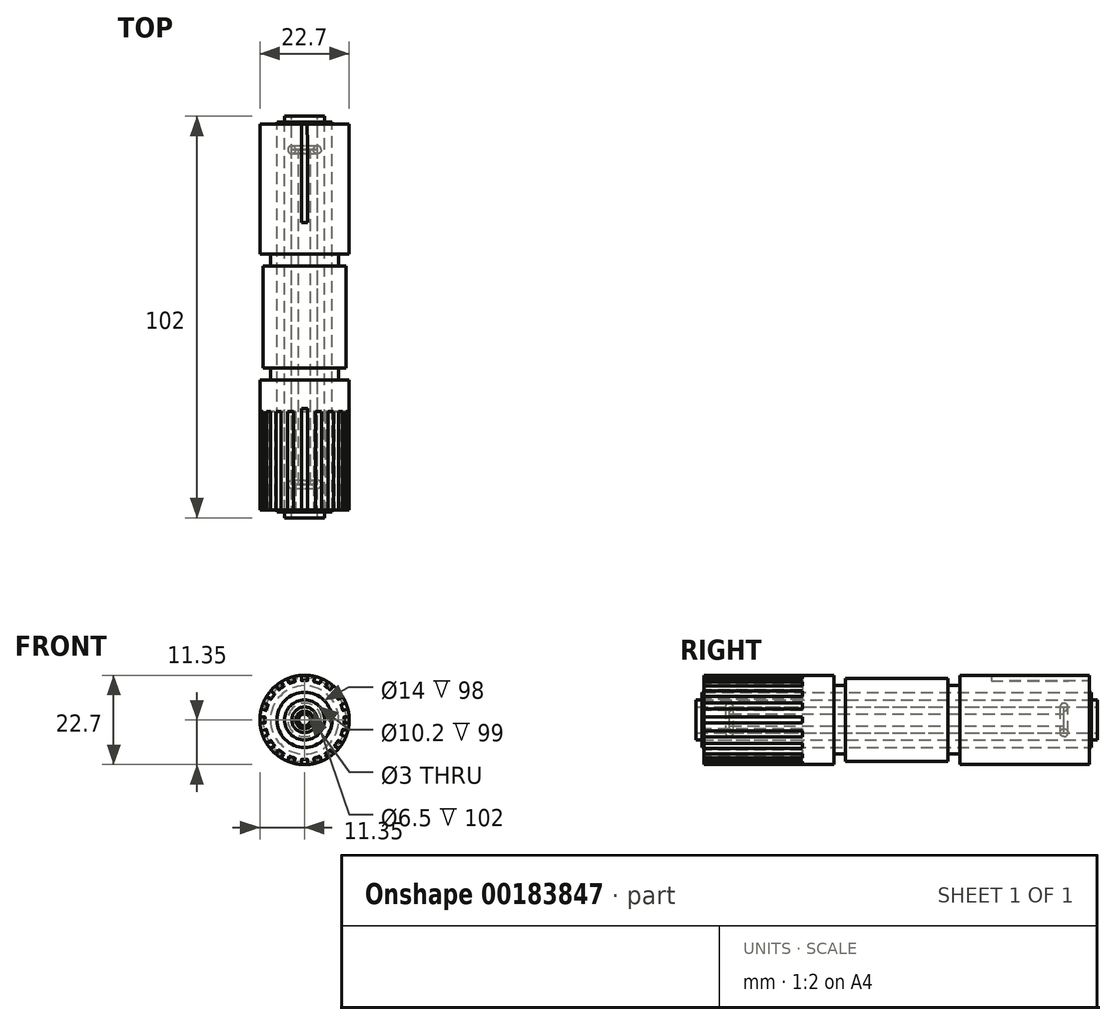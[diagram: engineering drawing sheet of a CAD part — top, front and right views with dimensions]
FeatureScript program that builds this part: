
annotation { "Feature Type Name" : "Feature", "Feature Type Description" : "" }
export const myFeature = defineFeature(function(context is Context, id is Id, definition is map)
    precondition{}
    {
        {
            var Q0;
            Q0=qCreatedBy(makeId("Front.planeOp"),FACE);
            var sketch = newSketch(context, id + "F0", { "sketchPlane" : qUnion([Q0])});
            skCircle(sketch, "E0", {"center": v(0, 0) * mm, "radius": 5.1 * mm});
            skCircle(sketch, "E1", {"center": v(0, 0) * mm, "radius": 7 * mm});
            skCircle(sketch, "E2", {"center": v(0, 0) * mm, "radius": 11.35 * mm});
            skCircle(sketch, "E3", {"center": v(0, 0) * mm, "radius": 8.7 * mm});
            skCircle(sketch, "E4", {"center": v(0, 0) * mm, "radius": 10.6 * mm});
            skCircle(sketch, "E5", {"center": v(0, 0) * mm, "radius": 10 * mm});
            skCircle(sketch, "E6", {"center": v(0, 0) * mm, "radius": 1.5 * mm});
            skCircle(sketch, "E7", {"center": v(0, 0) * mm, "radius": 3.25 * mm});
            skSolve(sketch);
        }
        {
            var Q0;
            Q0=makeQuery(id+"F0.imprint","IMPRINT",FACE,{"disambiguationData":[TD([[makeQuery(id+"F0.imprint","IMPRINT",EDGE,{"derivedFrom":sQuery(id+"F0.wireOp",EDGE,"E0")}),1.0]])]});
            extrude(context, id + "F1", {"entities" : qUnion([Q0]), "endBound" : BoundingType.SYMMETRIC, "depth" : 102 * mm});
        }
        {
            var Q0;
            Q0=makeQuery(id+"F0.imprint","IMPRINT",FACE,{"disambiguationData":[TD([[makeQuery(id+"F0.imprint","IMPRINT",EDGE,{"derivedFrom":sQuery(id+"F0.wireOp",EDGE,"E0")}),-1.0]])]});
            extrude(context, id + "F2", {"entities" : qUnion([Q0]), "endBound" : BoundingType.SYMMETRIC, "depth" : 99 * mm});
        }
        {
            var Q0;
            Q0=makeQuery(id+"F0.imprint","IMPRINT",FACE,{"disambiguationData":[TD([[makeQuery(id+"F0.imprint","IMPRINT",EDGE,{"derivedFrom":sQuery(id+"F0.wireOp",EDGE,"E6")}),-1.0]])]});
            extrude(context, id + "F3", {"entities" : qUnion([Q0]), "endBound" : BoundingType.SYMMETRIC, "depth" : 85 * mm});
        }
        {
            var Q0;
            Q0=makeQuery(id+"F0.imprint","IMPRINT",FACE,{"disambiguationData":[TD([[makeQuery(id+"F0.imprint","IMPRINT",EDGE,{"derivedFrom":sQuery(id+"F0.wireOp",EDGE,"E4")}),1.0]])]});
            var Q1;
            Q1=makeQuery(id+"F0.imprint","IMPRINT",FACE,{"disambiguationData":[TD([[makeQuery(id+"F0.imprint","IMPRINT",EDGE,{"derivedFrom":sQuery(id+"F0.wireOp",EDGE,"E3")}),-1.0]])]});
            var Q2;
            Q2=makeQuery(id+"F0.imprint","IMPRINT",FACE,{"disambiguationData":[TD([[makeQuery(id+"F0.imprint","IMPRINT",EDGE,{"derivedFrom":sQuery(id+"F0.wireOp",EDGE,"E1")}),-1.0]])]});
            var Q3;
            Q3=makeQuery(id+"F0.imprint","IMPRINT",FACE,{"disambiguationData":[TD([[makeQuery(id+"F0.imprint","IMPRINT",EDGE,{"derivedFrom":sQuery(id+"F0.wireOp",EDGE,"E2")}),1.0]])]});
            extrude(context, id + "F4", {"entities" : qUnion([Q0, Q1, Q2, Q3]), "endBound" : BoundingType.SYMMETRIC, "depth" : 98 * mm});
        }
        {
            var Q0;
            Q0=qCreatedBy(makeId("Front.planeOp"),FACE);
            var sketch = newSketch(context, id + "F5", { "sketchPlane" : qUnion([Q0])});
            skCircle(sketch, "E8.0", {"center": v(0, 0) * mm, "radius": 11.35 * mm});
            skCircle(sketch, "E9.0", {"center": v(0, 0) * mm, "radius": 8.7 * mm});
            skSolve(sketch);
        }
        {
            var Q0;
            Q0 = qSketchRegion(id + "F5", true);
            extrude(context, id + "F6", {"entities" : qUnion([Q0]), "operationType" : NewBodyOperationType.REMOVE, "endBound" : BoundingType.SYMMETRIC, "oppositeDirection" : true, "depth" : 32 * mm});
        }
        {
            var Q0;
            Q0=qCreatedBy(makeId("Front.planeOp"),FACE);
            var sketch = newSketch(context, id + "F7", { "sketchPlane" : qUnion([Q0])});
            skCircle(sketch, "E10.0", {"center": v(0, 0) * mm, "radius": 10.6 * mm});
            skCircle(sketch, "E11.0", {"center": v(0, 0) * mm, "radius": 8.7 * mm});
            skSolve(sketch);
        }
        {
            var Q0;
            Q0 = qSketchRegion(id + "F7", true);
            extrude(context, id + "F8", {"entities" : qUnion([Q0]), "operationType" : NewBodyOperationType.ADD, "endBound" : BoundingType.SYMMETRIC, "depth" : 26 * mm});
        }
        {
            var Q0;
            Q0=makeQuery(id+"F3.opExtrude","CAP_FACE",FACE,{"disambiguationData":[OSD([sQuery(id+"F0.wireOp",EDGE,"E6"),sQuery(id+"F0.wireOp",EDGE,"E7")])],"isStart":false});
            cPlane(context, id + "F9", {"entities" : qUnion([Q0]), "cplaneType" : CPlaneType.OFFSET, "offset" : 0 * mm, "width" : 150 * mm, "height" : 150 * mm});
        }
        {
            var Q0;
            Q0=qCreatedBy(id+"F9.planeOp",FACE);
            var sketch = newSketch(context, id + "F10", { "sketchPlane" : qUnion([Q0])});
            skCircle(sketch, "E12.0", {"center": v(0, 0) * mm, "radius": 3.25 * mm, "construction": true});
            skSolve(sketch);
        }
        {
            var Q0;
            Q0=qCreatedBy(makeId("Right.planeOp"),FACE);
            var sketch = newSketch(context, id + "F11", { "sketchPlane" : qUnion([Q0])});
            skLineSegment(sketch, "E13.0", {"start": v(-42.5, -3.25) * mm, "end": v(-42.5, 3.25) * mm, "construction": true});
            skCircle(sketch, "E14", {"center": v(-42.5, 3.25) * mm, "radius": 1 * mm});
            skSolve(sketch);
        }
        {
            var Q0;
            Q0 = qSketchRegion(id + "F11", true);
            var Q1;
            Q1=sQuery(id+"F11.wireOp",EDGE,"E14");
            var Q2;
            Q2=sQuery(id+"F10.wireOp",EDGE,"E12.0");
            revolve(context, id + "F12", {"entities" : qUnion([Q0]), "surfaceEntities" : qUnion([Q1]), "axis" : qUnion([Q2]), "revolveType" : RevolveType.FULL});
        }
        {
            var Q0;
            Q0=makeQuery(id+"F12.opRevolve","SWEPT_BODY",BODY,{"disambiguationData":[OSD([sQuery(id+"F11.wireOp",EDGE,"E14")])]});
            var Q1;
            Q1=qCreatedBy(makeId("Front.planeOp"),FACE);
            mirror(context, id + "F13", {"entities" : qUnion([Q0]), "mirrorPlane" : qUnion([Q1])});
        }
        {
            var Q0;
            Q0=makeQuery(id+"F4.opExtrude","CAP_FACE",FACE,{"disambiguationData":[OSD([sQuery(id+"F0.wireOp",EDGE,"E1"),sQuery(id+"F0.wireOp",EDGE,"E2")])],"isStart":false});
            cPlane(context, id + "F14", {"entities" : qUnion([Q0]), "cplaneType" : CPlaneType.OFFSET, "offset" : 0 * mm, "width" : 150 * mm, "height" : 150 * mm});
        }
        {
            var Q0;
            Q0=qCreatedBy(id+"F14.planeOp",FACE);
            var sketch = newSketch(context, id + "F15", { "sketchPlane" : qUnion([Q0])});
            skCircle(sketch, "E15.0", {"center": v(0, 0) * mm, "radius": 11.35 * mm, "construction": true});
            skCircle(sketch, "E16.0", {"center": v(0, 0) * mm, "radius": 10 * mm, "construction": true});
            skSolve(sketch);
        }
        {
            var Q0;
            Q0=qCreatedBy(makeId("Right.planeOp"),FACE);
            var sketch = newSketch(context, id + "F16", { "sketchPlane" : qUnion([Q0])});
            skLineSegment(sketch, "E17", {"start": v(-49, 10) * mm, "end": v(-49, 11.35) * mm});
            skPoint(sketch, "E18.0.start.orphan", {"position": v(-49, -10) * mm});
            skLineSegment(sketch, "E19", {"start": v(-49, 10.67) * mm, "end": v(-13.63, 12.53) * mm});
            skSolve(sketch);
        }
        {
            var Q0;
            Q0=qCreatedBy(id+"F14.planeOp",FACE);
            var sketch = newSketch(context, id + "F17", { "sketchPlane" : qUnion([Q0])});
            skLineSegment(sketch, "E20.0", {"start": v(0, 10) * mm, "end": v(0, 11.35) * mm, "construction": true});
            skPoint(sketch, "E21.middle", {"position": v(0, 10.68) * mm});
            skLineSegment(sketch, "E22.left", {"start": v(0.8, 11.32) * mm, "end": v(0.8, 10.08) * mm});
            skLineSegment(sketch, "E22.right", {"start": v(-0.8, 11.32) * mm, "end": v(-0.8, 10.08) * mm});
            skArc(sketch, "E23.0", {"start": v(0.7, 9.98) * mm, "mid": v(0, 10) * mm, "end": v(-0.7, 9.98) * mm});
            skPoint(sketch, "E24.orphan", {"position": v(-0.8, 9.9) * mm});
            skPoint(sketch, "E25.orphan", {"position": v(0.8, 9.9) * mm});
            skArc(sketch, "E26.0", {"start": v(0.8, 11.32) * mm, "mid": v(0, 11.35) * mm, "end": v(-0.8, 11.32) * mm});
            skPoint(sketch, "E27.orphan", {"position": v(-0.8, 11.44) * mm});
            skPoint(sketch, "E28.orphan", {"position": v(0.8, 11.44) * mm});
            skPoint(sketch, "E29.visualSharp", {"position": v(0.8, 9.97) * mm});
            skArc(sketch, "E29.filletArc", {"start": v(0.7, 9.98) * mm, "mid": v(0.77, 10) * mm, "end": v(0.8, 10.08) * mm});
            skPoint(sketch, "E30.visualSharp", {"position": v(-0.8, 9.97) * mm});
            skArc(sketch, "E30.filletArc", {"start": v(-0.8, 10.08) * mm, "mid": v(-0.77, 10) * mm, "end": v(-0.7, 9.98) * mm});
            skLineSegment(sketch, "E31.1.0", {"start": v(-4.26, 10.52) * mm, "end": v(-3.87, 9.34) * mm});
            skArc(sketch, "E31.1.1", {"start": v(-2.74, 11.01) * mm, "mid": v(-3.5, 10.8) * mm, "end": v(-4.26, 10.52) * mm});
            skLineSegment(sketch, "E31.1.2", {"start": v(-2.74, 11.01) * mm, "end": v(-2.35, 9.83) * mm});
            skArc(sketch, "E31.1.3", {"start": v(-2.42, 9.7) * mm, "mid": v(-3.1, 9.51) * mm, "end": v(-3.74, 9.27) * mm});
            skLineSegment(sketch, "E31.2.0", {"start": v(-7.3, 8.69) * mm, "end": v(-6.57, 7.68) * mm});
            skArc(sketch, "E31.2.1", {"start": v(-6, 9.63) * mm, "mid": v(-6.67, 9.18) * mm, "end": v(-7.3, 8.69) * mm});
            skLineSegment(sketch, "E31.2.2", {"start": v(-6, 9.63) * mm, "end": v(-5.28, 8.62) * mm});
            skArc(sketch, "E31.2.3", {"start": v(-5.3, 8.48) * mm, "mid": v(-5.88, 8.1) * mm, "end": v(-6.42, 7.66) * mm});
            skLineSegment(sketch, "E31.3.0", {"start": v(-9.63, 6) * mm, "end": v(-8.62, 5.28) * mm});
            skArc(sketch, "E31.3.1", {"start": v(-8.69, 7.3) * mm, "mid": v(-9.18, 6.67) * mm, "end": v(-9.63, 6) * mm});
            skLineSegment(sketch, "E31.3.2", {"start": v(-8.69, 7.3) * mm, "end": v(-7.68, 6.57) * mm});
            skArc(sketch, "E31.3.3", {"start": v(-7.66, 6.42) * mm, "mid": v(-8.1, 5.88) * mm, "end": v(-8.48, 5.3) * mm});
            skLineSegment(sketch, "E31.4.0", {"start": v(-11.01, 2.74) * mm, "end": v(-9.83, 2.35) * mm});
            skArc(sketch, "E31.4.1", {"start": v(-10.52, 4.26) * mm, "mid": v(-10.8, 3.5) * mm, "end": v(-11.01, 2.74) * mm});
            skLineSegment(sketch, "E31.4.2", {"start": v(-10.52, 4.26) * mm, "end": v(-9.34, 3.87) * mm});
            skArc(sketch, "E31.4.3", {"start": v(-9.27, 3.74) * mm, "mid": v(-9.51, 3.1) * mm, "end": v(-9.7, 2.42) * mm});
            skLineSegment(sketch, "E31.5.0", {"start": v(-11.32, -0.8) * mm, "end": v(-10.08, -0.8) * mm});
            skArc(sketch, "E31.5.1", {"start": v(-11.32, 0.8) * mm, "mid": v(-11.35, 0) * mm, "end": v(-11.32, -0.8) * mm});
            skLineSegment(sketch, "E31.5.2", {"start": v(-11.32, 0.8) * mm, "end": v(-10.08, 0.8) * mm});
            skArc(sketch, "E31.5.3", {"start": v(-9.98, 0.7) * mm, "mid": v(-10, 0) * mm, "end": v(-9.98, -0.7) * mm});
            skLineSegment(sketch, "E31.6.0", {"start": v(-10.52, -4.26) * mm, "end": v(-9.34, -3.87) * mm});
            skArc(sketch, "E31.6.1", {"start": v(-11.01, -2.74) * mm, "mid": v(-10.8, -3.5) * mm, "end": v(-10.52, -4.26) * mm});
            skLineSegment(sketch, "E31.6.2", {"start": v(-11.01, -2.74) * mm, "end": v(-9.83, -2.35) * mm});
            skArc(sketch, "E31.6.3", {"start": v(-9.7, -2.42) * mm, "mid": v(-9.51, -3.1) * mm, "end": v(-9.27, -3.74) * mm});
            skLineSegment(sketch, "E31.7.0", {"start": v(-8.69, -7.3) * mm, "end": v(-7.68, -6.57) * mm});
            skArc(sketch, "E31.7.1", {"start": v(-9.63, -6) * mm, "mid": v(-9.18, -6.67) * mm, "end": v(-8.69, -7.3) * mm});
            skLineSegment(sketch, "E31.7.2", {"start": v(-9.63, -6) * mm, "end": v(-8.62, -5.28) * mm});
            skArc(sketch, "E31.7.3", {"start": v(-8.48, -5.3) * mm, "mid": v(-8.1, -5.88) * mm, "end": v(-7.66, -6.42) * mm});
            skLineSegment(sketch, "E31.8.0", {"start": v(-6, -9.63) * mm, "end": v(-5.28, -8.62) * mm});
            skArc(sketch, "E31.8.1", {"start": v(-7.3, -8.69) * mm, "mid": v(-6.67, -9.18) * mm, "end": v(-6, -9.63) * mm});
            skLineSegment(sketch, "E31.8.2", {"start": v(-7.3, -8.69) * mm, "end": v(-6.57, -7.68) * mm});
            skArc(sketch, "E31.8.3", {"start": v(-6.42, -7.66) * mm, "mid": v(-5.88, -8.1) * mm, "end": v(-5.3, -8.48) * mm});
            skLineSegment(sketch, "E31.9.0", {"start": v(-2.74, -11.01) * mm, "end": v(-2.35, -9.83) * mm});
            skArc(sketch, "E31.9.1", {"start": v(-4.26, -10.52) * mm, "mid": v(-3.5, -10.8) * mm, "end": v(-2.74, -11.01) * mm});
            skLineSegment(sketch, "E31.9.2", {"start": v(-4.26, -10.52) * mm, "end": v(-3.87, -9.34) * mm});
            skArc(sketch, "E31.9.3", {"start": v(-3.74, -9.27) * mm, "mid": v(-3.1, -9.51) * mm, "end": v(-2.42, -9.7) * mm});
            skLineSegment(sketch, "E31.10.0", {"start": v(0.8, -11.32) * mm, "end": v(0.8, -10.08) * mm});
            skArc(sketch, "E31.10.1", {"start": v(-0.8, -11.32) * mm, "mid": v(0, -11.35) * mm, "end": v(0.8, -11.32) * mm});
            skLineSegment(sketch, "E31.10.2", {"start": v(-0.8, -11.32) * mm, "end": v(-0.8, -10.08) * mm});
            skArc(sketch, "E31.10.3", {"start": v(-0.7, -9.98) * mm, "mid": v(0, -10) * mm, "end": v(0.7, -9.98) * mm});
            skLineSegment(sketch, "E31.11.0", {"start": v(4.26, -10.52) * mm, "end": v(3.87, -9.34) * mm});
            skArc(sketch, "E31.11.1", {"start": v(2.74, -11.01) * mm, "mid": v(3.5, -10.8) * mm, "end": v(4.26, -10.52) * mm});
            skLineSegment(sketch, "E31.11.2", {"start": v(2.74, -11.01) * mm, "end": v(2.35, -9.83) * mm});
            skArc(sketch, "E31.11.3", {"start": v(2.42, -9.7) * mm, "mid": v(3.1, -9.51) * mm, "end": v(3.74, -9.27) * mm});
            skLineSegment(sketch, "E31.12.0", {"start": v(7.3, -8.69) * mm, "end": v(6.57, -7.68) * mm});
            skArc(sketch, "E31.12.1", {"start": v(6, -9.63) * mm, "mid": v(6.67, -9.18) * mm, "end": v(7.3, -8.69) * mm});
            skLineSegment(sketch, "E31.12.2", {"start": v(6, -9.63) * mm, "end": v(5.28, -8.62) * mm});
            skArc(sketch, "E31.12.3", {"start": v(5.3, -8.48) * mm, "mid": v(5.88, -8.1) * mm, "end": v(6.42, -7.66) * mm});
            skLineSegment(sketch, "E31.13.0", {"start": v(9.63, -6) * mm, "end": v(8.62, -5.28) * mm});
            skArc(sketch, "E31.13.1", {"start": v(8.69, -7.3) * mm, "mid": v(9.18, -6.67) * mm, "end": v(9.63, -6) * mm});
            skLineSegment(sketch, "E31.13.2", {"start": v(8.69, -7.3) * mm, "end": v(7.68, -6.57) * mm});
            skArc(sketch, "E31.13.3", {"start": v(7.66, -6.42) * mm, "mid": v(8.1, -5.88) * mm, "end": v(8.48, -5.3) * mm});
            skLineSegment(sketch, "E31.14.0", {"start": v(11.01, -2.74) * mm, "end": v(9.83, -2.35) * mm});
            skArc(sketch, "E31.14.1", {"start": v(10.52, -4.26) * mm, "mid": v(10.8, -3.5) * mm, "end": v(11.01, -2.74) * mm});
            skLineSegment(sketch, "E31.14.2", {"start": v(10.52, -4.26) * mm, "end": v(9.34, -3.87) * mm});
            skArc(sketch, "E31.14.3", {"start": v(9.27, -3.74) * mm, "mid": v(9.51, -3.1) * mm, "end": v(9.7, -2.42) * mm});
            skLineSegment(sketch, "E31.15.0", {"start": v(11.32, 0.8) * mm, "end": v(10.08, 0.8) * mm});
            skArc(sketch, "E31.15.1", {"start": v(11.32, -0.8) * mm, "mid": v(11.35, 0) * mm, "end": v(11.32, 0.8) * mm});
            skLineSegment(sketch, "E31.15.2", {"start": v(11.32, -0.8) * mm, "end": v(10.08, -0.8) * mm});
            skArc(sketch, "E31.15.3", {"start": v(9.98, -0.7) * mm, "mid": v(10, 0) * mm, "end": v(9.98, 0.7) * mm});
            skLineSegment(sketch, "E31.16.0", {"start": v(10.52, 4.26) * mm, "end": v(9.34, 3.87) * mm});
            skArc(sketch, "E31.16.1", {"start": v(11.01, 2.74) * mm, "mid": v(10.8, 3.5) * mm, "end": v(10.52, 4.26) * mm});
            skLineSegment(sketch, "E31.16.2", {"start": v(11.01, 2.74) * mm, "end": v(9.83, 2.35) * mm});
            skArc(sketch, "E31.16.3", {"start": v(9.7, 2.42) * mm, "mid": v(9.51, 3.1) * mm, "end": v(9.27, 3.74) * mm});
            skLineSegment(sketch, "E31.17.0", {"start": v(8.69, 7.3) * mm, "end": v(7.68, 6.57) * mm});
            skArc(sketch, "E31.17.1", {"start": v(9.63, 6) * mm, "mid": v(9.18, 6.67) * mm, "end": v(8.69, 7.3) * mm});
            skLineSegment(sketch, "E31.17.2", {"start": v(9.63, 6) * mm, "end": v(8.62, 5.28) * mm});
            skArc(sketch, "E31.17.3", {"start": v(8.48, 5.3) * mm, "mid": v(8.1, 5.88) * mm, "end": v(7.66, 6.42) * mm});
            skLineSegment(sketch, "E31.18.0", {"start": v(6, 9.63) * mm, "end": v(5.28, 8.62) * mm});
            skArc(sketch, "E31.18.1", {"start": v(7.3, 8.69) * mm, "mid": v(6.67, 9.18) * mm, "end": v(6, 9.63) * mm});
            skLineSegment(sketch, "E31.18.2", {"start": v(7.3, 8.69) * mm, "end": v(6.57, 7.68) * mm});
            skArc(sketch, "E31.18.3", {"start": v(6.42, 7.66) * mm, "mid": v(5.88, 8.1) * mm, "end": v(5.3, 8.48) * mm});
            skLineSegment(sketch, "E31.19.0", {"start": v(2.74, 11.01) * mm, "end": v(2.35, 9.83) * mm});
            skArc(sketch, "E31.19.1", {"start": v(4.26, 10.52) * mm, "mid": v(3.5, 10.8) * mm, "end": v(2.74, 11.01) * mm});
            skLineSegment(sketch, "E31.19.2", {"start": v(4.26, 10.52) * mm, "end": v(3.87, 9.34) * mm});
            skArc(sketch, "E31.19.3", {"start": v(3.74, 9.27) * mm, "mid": v(3.1, 9.51) * mm, "end": v(2.42, 9.7) * mm});
            skArc(sketch, "E32.1.0", {"start": v(-3.87, 9.34) * mm, "mid": v(-3.82, 9.28) * mm, "end": v(-3.74, 9.27) * mm});
            skArc(sketch, "E32.1.1", {"start": v(-2.42, 9.7) * mm, "mid": v(-2.36, 9.75) * mm, "end": v(-2.35, 9.83) * mm});
            skArc(sketch, "E32.2.0", {"start": v(-6.57, 7.68) * mm, "mid": v(-6.5, 7.64) * mm, "end": v(-6.42, 7.66) * mm});
            skArc(sketch, "E32.2.1", {"start": v(-5.3, 8.48) * mm, "mid": v(-5.26, 8.54) * mm, "end": v(-5.28, 8.62) * mm});
            skArc(sketch, "E32.3.0", {"start": v(-8.62, 5.28) * mm, "mid": v(-8.54, 5.26) * mm, "end": v(-8.48, 5.3) * mm});
            skArc(sketch, "E32.3.1", {"start": v(-7.66, 6.42) * mm, "mid": v(-7.64, 6.5) * mm, "end": v(-7.68, 6.57) * mm});
            skArc(sketch, "E32.4.0", {"start": v(-9.83, 2.35) * mm, "mid": v(-9.75, 2.36) * mm, "end": v(-9.7, 2.42) * mm});
            skArc(sketch, "E32.4.1", {"start": v(-9.27, 3.74) * mm, "mid": v(-9.28, 3.82) * mm, "end": v(-9.34, 3.87) * mm});
            skArc(sketch, "E32.5.0", {"start": v(-10.08, -0.8) * mm, "mid": v(-10, -0.77) * mm, "end": v(-9.98, -0.7) * mm});
            skArc(sketch, "E32.5.1", {"start": v(-9.98, 0.7) * mm, "mid": v(-10, 0.77) * mm, "end": v(-10.08, 0.8) * mm});
            skArc(sketch, "E32.6.0", {"start": v(-9.34, -3.87) * mm, "mid": v(-9.28, -3.82) * mm, "end": v(-9.27, -3.74) * mm});
            skArc(sketch, "E32.6.1", {"start": v(-9.7, -2.42) * mm, "mid": v(-9.75, -2.36) * mm, "end": v(-9.83, -2.35) * mm});
            skArc(sketch, "E32.7.0", {"start": v(-7.68, -6.57) * mm, "mid": v(-7.64, -6.5) * mm, "end": v(-7.66, -6.42) * mm});
            skArc(sketch, "E32.7.1", {"start": v(-8.48, -5.3) * mm, "mid": v(-8.54, -5.26) * mm, "end": v(-8.62, -5.28) * mm});
            skArc(sketch, "E32.8.0", {"start": v(-5.28, -8.62) * mm, "mid": v(-5.26, -8.54) * mm, "end": v(-5.3, -8.48) * mm});
            skArc(sketch, "E32.8.1", {"start": v(-6.42, -7.66) * mm, "mid": v(-6.5, -7.64) * mm, "end": v(-6.57, -7.68) * mm});
            skArc(sketch, "E32.9.0", {"start": v(-2.35, -9.83) * mm, "mid": v(-2.36, -9.75) * mm, "end": v(-2.42, -9.7) * mm});
            skArc(sketch, "E32.9.1", {"start": v(-3.74, -9.27) * mm, "mid": v(-3.82, -9.28) * mm, "end": v(-3.87, -9.34) * mm});
            skArc(sketch, "E32.10.0", {"start": v(0.8, -10.08) * mm, "mid": v(0.77, -10) * mm, "end": v(0.7, -9.98) * mm});
            skArc(sketch, "E32.10.1", {"start": v(-0.7, -9.98) * mm, "mid": v(-0.77, -10) * mm, "end": v(-0.8, -10.08) * mm});
            skArc(sketch, "E32.11.0", {"start": v(3.87, -9.34) * mm, "mid": v(3.82, -9.28) * mm, "end": v(3.74, -9.27) * mm});
            skArc(sketch, "E32.11.1", {"start": v(2.42, -9.7) * mm, "mid": v(2.36, -9.75) * mm, "end": v(2.35, -9.83) * mm});
            skArc(sketch, "E32.12.0", {"start": v(6.57, -7.68) * mm, "mid": v(6.5, -7.64) * mm, "end": v(6.42, -7.66) * mm});
            skArc(sketch, "E32.12.1", {"start": v(5.3, -8.48) * mm, "mid": v(5.26, -8.54) * mm, "end": v(5.28, -8.62) * mm});
            skArc(sketch, "E32.13.0", {"start": v(8.62, -5.28) * mm, "mid": v(8.54, -5.26) * mm, "end": v(8.48, -5.3) * mm});
            skArc(sketch, "E32.13.1", {"start": v(7.66, -6.42) * mm, "mid": v(7.64, -6.5) * mm, "end": v(7.68, -6.57) * mm});
            skArc(sketch, "E32.14.0", {"start": v(9.83, -2.35) * mm, "mid": v(9.75, -2.36) * mm, "end": v(9.7, -2.42) * mm});
            skArc(sketch, "E32.14.1", {"start": v(9.27, -3.74) * mm, "mid": v(9.28, -3.82) * mm, "end": v(9.34, -3.87) * mm});
            skArc(sketch, "E32.15.0", {"start": v(10.08, 0.8) * mm, "mid": v(10, 0.77) * mm, "end": v(9.98, 0.7) * mm});
            skArc(sketch, "E32.15.1", {"start": v(9.98, -0.7) * mm, "mid": v(10, -0.77) * mm, "end": v(10.08, -0.8) * mm});
            skArc(sketch, "E32.16.0", {"start": v(9.34, 3.87) * mm, "mid": v(9.28, 3.82) * mm, "end": v(9.27, 3.74) * mm});
            skArc(sketch, "E32.16.1", {"start": v(9.7, 2.42) * mm, "mid": v(9.75, 2.36) * mm, "end": v(9.83, 2.35) * mm});
            skArc(sketch, "E32.17.0", {"start": v(7.68, 6.57) * mm, "mid": v(7.64, 6.5) * mm, "end": v(7.66, 6.42) * mm});
            skArc(sketch, "E32.17.1", {"start": v(8.48, 5.3) * mm, "mid": v(8.54, 5.26) * mm, "end": v(8.62, 5.28) * mm});
            skArc(sketch, "E32.18.0", {"start": v(5.28, 8.62) * mm, "mid": v(5.26, 8.54) * mm, "end": v(5.3, 8.48) * mm});
            skArc(sketch, "E32.18.1", {"start": v(6.42, 7.66) * mm, "mid": v(6.5, 7.64) * mm, "end": v(6.57, 7.68) * mm});
            skArc(sketch, "E32.19.0", {"start": v(2.35, 9.83) * mm, "mid": v(2.36, 9.75) * mm, "end": v(2.42, 9.7) * mm});
            skArc(sketch, "E32.19.1", {"start": v(3.74, 9.27) * mm, "mid": v(3.82, 9.28) * mm, "end": v(3.87, 9.34) * mm});
            skSolve(sketch);
        }
        {
            var Q0;
            Q0=makeQuery(id+"F17.imprint","IMPRINT",FACE,{"disambiguationData":[TD([[makeQuery(id+"F17.imprint","IMPRINT",EDGE,{"derivedFrom":sQuery(id+"F17.wireOp",EDGE,"E22.left")}),-1.0]])]});
            var Q1;
            Q1=sQuery(id+"F16.wireOp",EDGE,"E19");
            sweep(context, id + "F18", {"operationType" : NewBodyOperationType.REMOVE, "profiles" : qUnion([Q0]), "path" : qUnion([Q1]), "keepProfileOrientation" : true});
        }
        {
            var Q0;
            {var subQ0=sQuery(id+"F5.wireOp",EDGE,"E9.0");Q0=makeQuery(id+"F8.boolean.opBoolean","SPLIT",FACE,{"disambiguationData":[TD([makeQuery(id+"F6.boolean.opBoolean","COPY",FACE,{"derivedFrom":makeQuery(id+"F6.opExtrude","CAP_FACE",FACE,{"disambiguationData":[OSD([sQuery(id+"F5.wireOp",EDGE,"E8.0"),subQ0])],"isStart":true})})])],"derivedFrom":makeQuery(id+"F6.boolean.opBoolean","COPY",FACE,{"derivedFrom":makeQuery(id+"F6.opExtrude","SWEPT_FACE",FACE,{"disambiguationData":[OSD([subQ0])]})})});}
            var Q1;
            {var subQ0=sQuery(id+"F5.wireOp",EDGE,"E9.0");Q1=makeQuery(id+"F8.boolean.opBoolean","SPLIT",FACE,{"disambiguationData":[TD([makeQuery(id+"F6.boolean.opBoolean","COPY",FACE,{"derivedFrom":makeQuery(id+"F6.opExtrude","CAP_FACE",FACE,{"disambiguationData":[OSD([sQuery(id+"F5.wireOp",EDGE,"E8.0"),subQ0])],"isStart":false})})])],"derivedFrom":makeQuery(id+"F6.boolean.opBoolean","COPY",FACE,{"derivedFrom":makeQuery(id+"F6.opExtrude","SWEPT_FACE",FACE,{"disambiguationData":[OSD([subQ0])]})})});}
            fillet(context, id + "F19", {"entities" : qUnion([Q0, Q1]), "radius" : 0.2 * mm, "tangentPropagation" : true, "allowEdgeOverflow" : false});
        }
        {
            var Q0;
            Q0=makeQuery(id+"F17.imprint","IMPRINT",FACE,{"disambiguationData":[TD([[makeQuery(id+"F17.imprint","IMPRINT",EDGE,{"derivedFrom":sQuery(id+"F17.wireOp",EDGE,"E31.3.0")}),1.0]])]});
            var Q1;
            Q1=makeQuery(id+"F17.imprint","IMPRINT",FACE,{"disambiguationData":[TD([[makeQuery(id+"F17.imprint","IMPRINT",EDGE,{"derivedFrom":sQuery(id+"F17.wireOp",EDGE,"E31.4.0")}),1.0]])]});
            var Q2;
            Q2=makeQuery(id+"F17.imprint","IMPRINT",FACE,{"disambiguationData":[TD([[makeQuery(id+"F17.imprint","IMPRINT",EDGE,{"derivedFrom":sQuery(id+"F17.wireOp",EDGE,"E31.5.0")}),1.0]])]});
            var Q3;
            Q3=makeQuery(id+"F17.imprint","IMPRINT",FACE,{"disambiguationData":[TD([[makeQuery(id+"F17.imprint","IMPRINT",EDGE,{"derivedFrom":sQuery(id+"F17.wireOp",EDGE,"E31.6.0")}),1.0]])]});
            var Q4;
            Q4=makeQuery(id+"F17.imprint","IMPRINT",FACE,{"disambiguationData":[TD([[makeQuery(id+"F17.imprint","IMPRINT",EDGE,{"derivedFrom":sQuery(id+"F17.wireOp",EDGE,"E31.7.0")}),1.0]])]});
            var Q5;
            Q5=makeQuery(id+"F17.imprint","IMPRINT",FACE,{"disambiguationData":[TD([[makeQuery(id+"F17.imprint","IMPRINT",EDGE,{"derivedFrom":sQuery(id+"F17.wireOp",EDGE,"E31.8.0")}),1.0]])]});
            var Q6;
            Q6=makeQuery(id+"F17.imprint","IMPRINT",FACE,{"disambiguationData":[TD([[makeQuery(id+"F17.imprint","IMPRINT",EDGE,{"derivedFrom":sQuery(id+"F17.wireOp",EDGE,"E31.9.0")}),1.0]])]});
            var Q7;
            Q7=makeQuery(id+"F17.imprint","IMPRINT",FACE,{"disambiguationData":[TD([[makeQuery(id+"F17.imprint","IMPRINT",EDGE,{"derivedFrom":sQuery(id+"F17.wireOp",EDGE,"E31.10.0")}),1.0]])]});
            var Q8;
            Q8=makeQuery(id+"F17.imprint","IMPRINT",FACE,{"disambiguationData":[TD([[makeQuery(id+"F17.imprint","IMPRINT",EDGE,{"derivedFrom":sQuery(id+"F17.wireOp",EDGE,"E31.11.0")}),1.0]])]});
            var Q9;
            Q9=makeQuery(id+"F17.imprint","IMPRINT",FACE,{"disambiguationData":[TD([[makeQuery(id+"F17.imprint","IMPRINT",EDGE,{"derivedFrom":sQuery(id+"F17.wireOp",EDGE,"E31.12.0")}),1.0]])]});
            var Q10;
            Q10=makeQuery(id+"F17.imprint","IMPRINT",FACE,{"disambiguationData":[TD([[makeQuery(id+"F17.imprint","IMPRINT",EDGE,{"derivedFrom":sQuery(id+"F17.wireOp",EDGE,"E31.13.0")}),1.0]])]});
            var Q11;
            Q11=makeQuery(id+"F17.imprint","IMPRINT",FACE,{"disambiguationData":[TD([[makeQuery(id+"F17.imprint","IMPRINT",EDGE,{"derivedFrom":sQuery(id+"F17.wireOp",EDGE,"E31.14.0")}),1.0]])]});
            var Q12;
            Q12=makeQuery(id+"F17.imprint","IMPRINT",FACE,{"disambiguationData":[TD([[makeQuery(id+"F17.imprint","IMPRINT",EDGE,{"derivedFrom":sQuery(id+"F17.wireOp",EDGE,"E31.15.0")}),1.0]])]});
            var Q13;
            Q13=makeQuery(id+"F17.imprint","IMPRINT",FACE,{"disambiguationData":[TD([[makeQuery(id+"F17.imprint","IMPRINT",EDGE,{"derivedFrom":sQuery(id+"F17.wireOp",EDGE,"E31.16.0")}),1.0]])]});
            var Q14;
            Q14=makeQuery(id+"F17.imprint","IMPRINT",FACE,{"disambiguationData":[TD([[makeQuery(id+"F17.imprint","IMPRINT",EDGE,{"derivedFrom":sQuery(id+"F17.wireOp",EDGE,"E31.17.0")}),1.0]])]});
            var Q15;
            Q15=makeQuery(id+"F17.imprint","IMPRINT",FACE,{"disambiguationData":[TD([[makeQuery(id+"F17.imprint","IMPRINT",EDGE,{"derivedFrom":sQuery(id+"F17.wireOp",EDGE,"E31.18.0")}),1.0]])]});
            var Q16;
            Q16=makeQuery(id+"F17.imprint","IMPRINT",FACE,{"disambiguationData":[TD([[makeQuery(id+"F17.imprint","IMPRINT",EDGE,{"derivedFrom":sQuery(id+"F17.wireOp",EDGE,"E31.19.0")}),1.0]])]});
            var Q17;
            Q17=makeQuery(id+"F17.imprint","IMPRINT",FACE,{"disambiguationData":[TD([[makeQuery(id+"F17.imprint","IMPRINT",EDGE,{"derivedFrom":sQuery(id+"F17.wireOp",EDGE,"E31.1.0")}),1.0]])]});
            var Q18;
            Q18=makeQuery(id+"F17.imprint","IMPRINT",FACE,{"disambiguationData":[TD([[makeQuery(id+"F17.imprint","IMPRINT",EDGE,{"derivedFrom":sQuery(id+"F17.wireOp",EDGE,"E31.2.0")}),1.0]])]});
            extrude(context, id + "F20", {"entities" : qUnion([Q0, Q1, Q2, Q3, Q4, Q5, Q6, Q7, Q8, Q9, Q10, Q11, Q12, Q13, Q14, Q15, Q16, Q17, Q18]), "operationType" : NewBodyOperationType.REMOVE, "oppositeDirection" : true, "depth" : 25 * mm});
        }
        {
            var Q0;
            Q0=makeQuery(id+"F4.opExtrude","CAP_FACE",FACE,{"disambiguationData":[OSD([sQuery(id+"F0.wireOp",EDGE,"E1"),sQuery(id+"F0.wireOp",EDGE,"E2")])],"isStart":true});
            var sketch = newSketch(context, id + "F21", { "sketchPlane" : qUnion([Q0])});
            skLineSegment(sketch, "E33.0", {"start": v(0.8, 11.32) * mm, "end": v(0.8, 10.08) * mm});
            skArc(sketch, "E33.1", {"start": v(2.74, 11.01) * mm, "mid": v(3.5, 10.8) * mm, "end": v(4.26, 10.52) * mm});
            skArc(sketch, "E33.2", {"start": v(-6.42, 7.66) * mm, "mid": v(-5.88, 8.1) * mm, "end": v(-5.3, 8.48) * mm});
            skLineSegment(sketch, "E33.3", {"start": v(8.69, 7.3) * mm, "end": v(7.68, 6.57) * mm});
            skArc(sketch, "E33.4", {"start": v(6, 9.63) * mm, "mid": v(6.67, 9.18) * mm, "end": v(7.3, 8.69) * mm});
            skLineSegment(sketch, "E33.5", {"start": v(0.8, -11.32) * mm, "end": v(0.8, -10.08) * mm});
            skLineSegment(sketch, "E33.6", {"start": v(-2.74, 11.01) * mm, "end": v(-2.35, 9.83) * mm});
            skLineSegment(sketch, "E33.7", {"start": v(-10.52, -4.26) * mm, "end": v(-9.34, -3.87) * mm});
            skLineSegment(sketch, "E33.8", {"start": v(11.01, -2.74) * mm, "end": v(9.83, -2.35) * mm});
            skArc(sketch, "E33.9", {"start": v(5.3, 8.48) * mm, "mid": v(5.88, 8.1) * mm, "end": v(6.42, 7.66) * mm});
            skLineSegment(sketch, "E33.10", {"start": v(2.74, 11.01) * mm, "end": v(2.35, 9.83) * mm});
            skLineSegment(sketch, "E33.11", {"start": v(-2.74, -11.01) * mm, "end": v(-2.35, -9.83) * mm});
            skArc(sketch, "E33.12", {"start": v(9.7, -2.42) * mm, "mid": v(9.51, -3.1) * mm, "end": v(9.27, -3.74) * mm});
            skArc(sketch, "E33.13", {"start": v(2.42, 9.7) * mm, "mid": v(3.1, 9.51) * mm, "end": v(3.74, 9.27) * mm});
            skArc(sketch, "E33.14", {"start": v(9.63, -6) * mm, "mid": v(9.18, -6.67) * mm, "end": v(8.69, -7.3) * mm});
            skLineSegment(sketch, "E33.15", {"start": v(-4.26, 10.52) * mm, "end": v(-3.87, 9.34) * mm});
            skArc(sketch, "E33.16", {"start": v(-11.32, -0.8) * mm, "mid": v(-11.35, 0) * mm, "end": v(-11.32, 0.8) * mm});
            skLineSegment(sketch, "E33.17", {"start": v(-7.3, 8.69) * mm, "end": v(-6.57, 7.68) * mm});
            skLineSegment(sketch, "E33.18", {"start": v(7.3, 8.69) * mm, "end": v(6.57, 7.68) * mm});
            skArc(sketch, "E33.19", {"start": v(-4.26, 10.52) * mm, "mid": v(-3.5, 10.8) * mm, "end": v(-2.74, 11.01) * mm});
            skLineSegment(sketch, "E33.20", {"start": v(-11.32, -0.8) * mm, "end": v(-10.08, -0.8) * mm});
            skArc(sketch, "E33.21", {"start": v(-2.74, -11.01) * mm, "mid": v(-3.5, -10.8) * mm, "end": v(-4.26, -10.52) * mm});
            skArc(sketch, "E33.22", {"start": v(0.7, -9.98) * mm, "mid": v(0, -10) * mm, "end": v(-0.7, -9.98) * mm});
            skLineSegment(sketch, "E33.23", {"start": v(-0.8, 11.32) * mm, "end": v(-0.8, 10.08) * mm});
            skLineSegment(sketch, "E33.24", {"start": v(-4.26, -10.52) * mm, "end": v(-3.87, -9.34) * mm});
            skLineSegment(sketch, "E33.25", {"start": v(9.63, -6) * mm, "end": v(8.62, -5.28) * mm});
            skLineSegment(sketch, "E33.26", {"start": v(9.63, 6) * mm, "end": v(8.62, 5.28) * mm});
            skLineSegment(sketch, "E33.27", {"start": v(8.69, -7.3) * mm, "end": v(7.68, -6.57) * mm});
            skLineSegment(sketch, "E33.28", {"start": v(6, 9.63) * mm, "end": v(5.28, 8.62) * mm});
            skLineSegment(sketch, "E33.29", {"start": v(-11.32, 0.8) * mm, "end": v(-10.08, 0.8) * mm});
            skLineSegment(sketch, "E33.30", {"start": v(4.26, 10.52) * mm, "end": v(3.87, 9.34) * mm});
            skArc(sketch, "E33.31", {"start": v(8.69, 7.3) * mm, "mid": v(9.18, 6.67) * mm, "end": v(9.63, 6) * mm});
            skArc(sketch, "E33.32", {"start": v(-9.27, -3.74) * mm, "mid": v(-9.51, -3.1) * mm, "end": v(-9.7, -2.42) * mm});
            skArc(sketch, "E33.33", {"start": v(-9.98, -0.7) * mm, "mid": v(-10, 0) * mm, "end": v(-9.98, 0.7) * mm});
            skArc(sketch, "E33.34", {"start": v(-2.42, -9.7) * mm, "mid": v(-3.1, -9.51) * mm, "end": v(-3.74, -9.27) * mm});
            skArc(sketch, "E33.35", {"start": v(8.48, -5.3) * mm, "mid": v(8.1, -5.88) * mm, "end": v(7.66, -6.42) * mm});
            skArc(sketch, "E33.36", {"start": v(7.66, 6.42) * mm, "mid": v(8.1, 5.88) * mm, "end": v(8.48, 5.3) * mm});
            skArc(sketch, "E33.37", {"start": v(-3.74, 9.27) * mm, "mid": v(-3.1, 9.51) * mm, "end": v(-2.42, 9.7) * mm});
            skLineSegment(sketch, "E33.38", {"start": v(-10.52, 4.26) * mm, "end": v(-9.34, 3.87) * mm});
            skLineSegment(sketch, "E33.39", {"start": v(-7.3, -8.69) * mm, "end": v(-6.57, -7.68) * mm});
            skLineSegment(sketch, "E33.40", {"start": v(6, -9.63) * mm, "end": v(5.28, -8.62) * mm});
            skLineSegment(sketch, "E33.41", {"start": v(11.01, 2.74) * mm, "end": v(9.83, 2.35) * mm});
            skArc(sketch, "E33.42", {"start": v(-11.01, 2.74) * mm, "mid": v(-10.8, 3.5) * mm, "end": v(-10.52, 4.26) * mm});
            skArc(sketch, "E33.43", {"start": v(-6, -9.63) * mm, "mid": v(-6.67, -9.18) * mm, "end": v(-7.3, -8.69) * mm});
            skArc(sketch, "E33.44", {"start": v(7.3, -8.69) * mm, "mid": v(6.67, -9.18) * mm, "end": v(6, -9.63) * mm});
            skArc(sketch, "E33.45", {"start": v(10.52, 4.26) * mm, "mid": v(10.8, 3.5) * mm, "end": v(11.01, 2.74) * mm});
            skLineSegment(sketch, "E33.46", {"start": v(-11.01, 2.74) * mm, "end": v(-9.83, 2.35) * mm});
            skLineSegment(sketch, "E33.47", {"start": v(-6, -9.63) * mm, "end": v(-5.28, -8.62) * mm});
            skLineSegment(sketch, "E33.48", {"start": v(7.3, -8.69) * mm, "end": v(6.57, -7.68) * mm});
            skLineSegment(sketch, "E33.49", {"start": v(10.52, 4.26) * mm, "end": v(9.34, 3.87) * mm});
            skArc(sketch, "E33.50", {"start": v(-9.7, 2.42) * mm, "mid": v(-9.51, 3.1) * mm, "end": v(-9.27, 3.74) * mm});
            skArc(sketch, "E33.51", {"start": v(-5.3, -8.48) * mm, "mid": v(-5.88, -8.1) * mm, "end": v(-6.42, -7.66) * mm});
            skArc(sketch, "E33.52", {"start": v(6.42, -7.66) * mm, "mid": v(5.88, -8.1) * mm, "end": v(5.3, -8.48) * mm});
            skArc(sketch, "E33.53", {"start": v(9.27, 3.74) * mm, "mid": v(9.51, 3.1) * mm, "end": v(9.7, 2.42) * mm});
            skLineSegment(sketch, "E33.54", {"start": v(2.74, -11.01) * mm, "end": v(2.35, -9.83) * mm});
            skLineSegment(sketch, "E33.55", {"start": v(11.32, -0.8) * mm, "end": v(10.08, -0.8) * mm});
            skLineSegment(sketch, "E33.56", {"start": v(-8.69, 7.3) * mm, "end": v(-7.68, 6.57) * mm});
            skLineSegment(sketch, "E33.57", {"start": v(-9.63, -6) * mm, "end": v(-8.62, -5.28) * mm});
            skArc(sketch, "E33.58", {"start": v(4.26, -10.52) * mm, "mid": v(3.5, -10.8) * mm, "end": v(2.74, -11.01) * mm});
            skArc(sketch, "E33.59", {"start": v(11.32, 0.8) * mm, "mid": v(11.35, 0) * mm, "end": v(11.32, -0.8) * mm});
            skArc(sketch, "E33.60", {"start": v(-9.63, 6) * mm, "mid": v(-9.18, 6.67) * mm, "end": v(-8.69, 7.3) * mm});
            skArc(sketch, "E33.61", {"start": v(-8.69, -7.3) * mm, "mid": v(-9.18, -6.67) * mm, "end": v(-9.63, -6) * mm});
            skLineSegment(sketch, "E33.62", {"start": v(4.26, -10.52) * mm, "end": v(3.87, -9.34) * mm});
            skLineSegment(sketch, "E33.63", {"start": v(11.32, 0.8) * mm, "end": v(10.08, 0.8) * mm});
            skLineSegment(sketch, "E33.64", {"start": v(-9.63, 6) * mm, "end": v(-8.62, 5.28) * mm});
            skLineSegment(sketch, "E33.65", {"start": v(-8.69, -7.3) * mm, "end": v(-7.68, -6.57) * mm});
            skArc(sketch, "E33.66", {"start": v(3.74, -9.27) * mm, "mid": v(3.1, -9.51) * mm, "end": v(2.42, -9.7) * mm});
            skArc(sketch, "E33.67", {"start": v(9.98, 0.7) * mm, "mid": v(10, 0) * mm, "end": v(9.98, -0.7) * mm});
            skArc(sketch, "E33.68", {"start": v(-8.48, 5.3) * mm, "mid": v(-8.1, 5.88) * mm, "end": v(-7.66, 6.42) * mm});
            skArc(sketch, "E33.69", {"start": v(-7.66, -6.42) * mm, "mid": v(-8.1, -5.88) * mm, "end": v(-8.48, -5.3) * mm});
            skLineSegment(sketch, "E33.70", {"start": v(-0.8, -11.32) * mm, "end": v(-0.8, -10.08) * mm});
            skLineSegment(sketch, "E33.71", {"start": v(10.52, -4.26) * mm, "end": v(9.34, -3.87) * mm});
            skLineSegment(sketch, "E33.72", {"start": v(-6, 9.63) * mm, "end": v(-5.28, 8.62) * mm});
            skLineSegment(sketch, "E33.73", {"start": v(-11.01, -2.74) * mm, "end": v(-9.83, -2.35) * mm});
            skArc(sketch, "E33.74", {"start": v(0.8, -11.32) * mm, "mid": v(0, -11.35) * mm, "end": v(-0.8, -11.32) * mm});
            skArc(sketch, "E33.75", {"start": v(11.01, -2.74) * mm, "mid": v(10.8, -3.5) * mm, "end": v(10.52, -4.26) * mm});
            skArc(sketch, "E33.76", {"start": v(-7.3, 8.69) * mm, "mid": v(-6.67, 9.18) * mm, "end": v(-6, 9.63) * mm});
            skArc(sketch, "E33.77", {"start": v(-10.52, -4.26) * mm, "mid": v(-10.8, -3.5) * mm, "end": v(-11.01, -2.74) * mm});
            skArc(sketch, "E33.78", {"start": v(-2.74, 11.01) * mm, "mid": v(1.78, -11.21) * mm, "end": v(-0.8, 11.32) * mm});
            skArc(sketch, "E33.79", {"start": v(-0.8, -11.32) * mm, "mid": v(-1.78, -11.21) * mm, "end": v(-2.74, -11.01) * mm});
            skCircle(sketch, "E33.81", {"center": v(0, 0) * mm, "radius": 3.25 * mm});
            skLineSegment(sketch, "E33.83", {"start": v(0, 10) * mm, "end": v(0, 11.35) * mm});
            skArc(sketch, "E33.84", {"start": v(-0.7, 9.98) * mm, "mid": v(0, 10) * mm, "end": v(0.7, 9.98) * mm});
            skArc(sketch, "E33.85", {"start": v(-0.8, 11.32) * mm, "mid": v(0, 11.35) * mm, "end": v(0.8, 11.32) * mm});
            skCircle(sketch, "E33.86", {"center": v(0, 0) * mm, "radius": 7 * mm});
            skCircle(sketch, "E33.87", {"center": v(0, 0) * mm, "radius": 11.35 * mm});
            skCircle(sketch, "E33.88", {"center": v(0, 0) * mm, "radius": 8.9 * mm});
            skCircle(sketch, "E33.89", {"center": v(0, 0) * mm, "radius": 8.7 * mm});
            skCircle(sketch, "E33.90", {"center": v(0, 0) * mm, "radius": 5.1 * mm});
            skCircle(sketch, "E33.91", {"center": v(0, 0) * mm, "radius": 1.5 * mm});
            skArc(sketch, "E33.92", {"start": v(5.28, -8.62) * mm, "mid": v(5.26, -8.54) * mm, "end": v(5.3, -8.48) * mm});
            skArc(sketch, "E33.93", {"start": v(9.34, -3.87) * mm, "mid": v(9.28, -3.82) * mm, "end": v(9.27, -3.74) * mm});
            skArc(sketch, "E33.94", {"start": v(9.7, -2.42) * mm, "mid": v(9.75, -2.36) * mm, "end": v(9.83, -2.35) * mm});
            skArc(sketch, "E33.95", {"start": v(-9.83, -2.35) * mm, "mid": v(-9.75, -2.36) * mm, "end": v(-9.7, -2.42) * mm});
            skArc(sketch, "E33.96", {"start": v(-9.7, 2.42) * mm, "mid": v(-9.75, 2.36) * mm, "end": v(-9.83, 2.35) * mm});
            skArc(sketch, "E33.97", {"start": v(-5.28, 8.62) * mm, "mid": v(-5.26, 8.54) * mm, "end": v(-5.3, 8.48) * mm});
            skArc(sketch, "E33.98", {"start": v(6.57, 7.68) * mm, "mid": v(6.5, 7.64) * mm, "end": v(6.42, 7.66) * mm});
            skArc(sketch, "E33.99", {"start": v(5.3, 8.48) * mm, "mid": v(5.26, 8.54) * mm, "end": v(5.28, 8.62) * mm});
            skArc(sketch, "E33.100", {"start": v(9.83, 2.35) * mm, "mid": v(9.75, 2.36) * mm, "end": v(9.7, 2.42) * mm});
            skArc(sketch, "E33.101", {"start": v(-5.3, -8.48) * mm, "mid": v(-5.26, -8.54) * mm, "end": v(-5.28, -8.62) * mm});
            skArc(sketch, "E33.102", {"start": v(9.27, 3.74) * mm, "mid": v(9.28, 3.82) * mm, "end": v(9.34, 3.87) * mm});
            skArc(sketch, "E33.103", {"start": v(10.08, -0.8) * mm, "mid": v(10, -0.77) * mm, "end": v(9.98, -0.7) * mm});
            skCircle(sketch, "E33.104", {"center": v(0, 0) * mm, "radius": 7 * mm});
            skArc(sketch, "E33.105", {"start": v(-2.5, 10.3) * mm, "mid": v(1.66, -10.47) * mm, "end": v(-0.8, 10.57) * mm});
            skCircle(sketch, "E33.106", {"center": v(0, 0) * mm, "radius": 8.9 * mm});
            skCircle(sketch, "E33.107", {"center": v(0, 0) * mm, "radius": 11.35 * mm});
            skCircle(sketch, "E33.108", {"center": v(0, 0) * mm, "radius": 8.7 * mm});
            skCircle(sketch, "E33.109", {"center": v(0, 0) * mm, "radius": 5.1 * mm});
            skCircle(sketch, "E33.110", {"center": v(0, 0) * mm, "radius": 3.25 * mm});
            skArc(sketch, "E33.112", {"start": v(-9.34, 3.87) * mm, "mid": v(-9.28, 3.82) * mm, "end": v(-9.27, 3.74) * mm});
            skArc(sketch, "E33.113", {"start": v(-9.98, -0.7) * mm, "mid": v(-10, -0.77) * mm, "end": v(-10.08, -0.8) * mm});
            skArc(sketch, "E33.114", {"start": v(7.68, -6.57) * mm, "mid": v(7.64, -6.5) * mm, "end": v(7.66, -6.42) * mm});
            skArc(sketch, "E33.115", {"start": v(-9.27, -3.74) * mm, "mid": v(-9.28, -3.82) * mm, "end": v(-9.34, -3.87) * mm});
            skArc(sketch, "E33.116", {"start": v(6.42, -7.66) * mm, "mid": v(6.5, -7.64) * mm, "end": v(6.57, -7.68) * mm});
            skArc(sketch, "E33.117", {"start": v(-7.68, 6.57) * mm, "mid": v(-7.64, 6.5) * mm, "end": v(-7.66, 6.42) * mm});
            skArc(sketch, "E33.118", {"start": v(2.35, -9.83) * mm, "mid": v(2.36, -9.75) * mm, "end": v(2.42, -9.7) * mm});
            skArc(sketch, "E33.119", {"start": v(3.87, 9.34) * mm, "mid": v(3.82, 9.28) * mm, "end": v(3.74, 9.27) * mm});
            skArc(sketch, "E33.120", {"start": v(-8.48, 5.3) * mm, "mid": v(-8.54, 5.26) * mm, "end": v(-8.62, 5.28) * mm});
            skArc(sketch, "E33.121", {"start": v(3.74, -9.27) * mm, "mid": v(3.82, -9.28) * mm, "end": v(3.87, -9.34) * mm});
            skArc(sketch, "E33.122", {"start": v(2.42, 9.7) * mm, "mid": v(2.36, 9.75) * mm, "end": v(2.35, 9.83) * mm});
            skArc(sketch, "E33.123", {"start": v(-0.8, -10.08) * mm, "mid": v(-0.77, -10) * mm, "end": v(-0.7, -9.98) * mm});
            skArc(sketch, "E33.124", {"start": v(-6.42, 7.66) * mm, "mid": v(-6.5, 7.64) * mm, "end": v(-6.57, 7.68) * mm});
            skArc(sketch, "E33.125", {"start": v(-3.87, -9.34) * mm, "mid": v(-3.82, -9.28) * mm, "end": v(-3.74, -9.27) * mm});
            skArc(sketch, "E33.126", {"start": v(-2.35, 9.83) * mm, "mid": v(-2.36, 9.75) * mm, "end": v(-2.42, 9.7) * mm});
            skArc(sketch, "E33.127", {"start": v(-2.42, -9.7) * mm, "mid": v(-2.36, -9.75) * mm, "end": v(-2.35, -9.83) * mm});
            skArc(sketch, "E33.128", {"start": v(7.66, 6.42) * mm, "mid": v(7.64, 6.5) * mm, "end": v(7.68, 6.57) * mm});
            skArc(sketch, "E33.129", {"start": v(-3.74, 9.27) * mm, "mid": v(-3.82, 9.28) * mm, "end": v(-3.87, 9.34) * mm});
            skArc(sketch, "E33.130", {"start": v(-8.62, -5.28) * mm, "mid": v(-8.54, -5.26) * mm, "end": v(-8.48, -5.3) * mm});
            skArc(sketch, "E33.131", {"start": v(-7.66, -6.42) * mm, "mid": v(-7.64, -6.5) * mm, "end": v(-7.68, -6.57) * mm});
            skArc(sketch, "E33.132", {"start": v(9.98, 0.7) * mm, "mid": v(10, 0.77) * mm, "end": v(10.08, 0.8) * mm});
            skLineSegment(sketch, "E33.133", {"start": v(6, -9.63) * mm, "end": v(5.28, -8.62) * mm});
            skArc(sketch, "E33.134", {"start": v(8.69, 7.3) * mm, "mid": v(9.18, 6.67) * mm, "end": v(9.63, 6) * mm});
            skCircle(sketch, "E33.135", {"center": v(0, 0) * mm, "radius": 10.6 * mm});
            skArc(sketch, "E33.136", {"start": v(0.8, -11.32) * mm, "mid": v(0, -11.35) * mm, "end": v(-0.8, -11.32) * mm});
            skCircle(sketch, "E33.137", {"center": v(0, 0) * mm, "radius": 8.7 * mm});
            skLineSegment(sketch, "E33.138", {"start": v(6, 9.63) * mm, "end": v(5.28, 8.62) * mm});
            skArc(sketch, "E33.139", {"start": v(9.63, -6) * mm, "mid": v(9.18, -6.67) * mm, "end": v(8.69, -7.3) * mm});
            skArc(sketch, "E33.140", {"start": v(-10.52, 4.26) * mm, "mid": v(-10.11, 5.15) * mm, "end": v(-9.63, 6) * mm});
            skLineSegment(sketch, "E33.141", {"start": v(-8.69, 7.3) * mm, "end": v(-7.68, 6.57) * mm});
            skArc(sketch, "E33.142", {"start": v(-7.3, 8.69) * mm, "mid": v(-6.67, 9.18) * mm, "end": v(-6, 9.63) * mm});
            skArc(sketch, "E33.143", {"start": v(2.74, 11.01) * mm, "mid": v(3.5, 10.8) * mm, "end": v(4.26, 10.52) * mm});
            skArc(sketch, "E33.144", {"start": v(-10.52, -4.26) * mm, "mid": v(-10.8, -3.5) * mm, "end": v(-11.01, -2.74) * mm});
            skArc(sketch, "E33.145", {"start": v(4.26, 10.52) * mm, "mid": v(5.15, 10.11) * mm, "end": v(6, 9.63) * mm});
            skLineSegment(sketch, "E33.146", {"start": v(-4.26, -10.52) * mm, "end": v(-3.87, -9.34) * mm});
            skArc(sketch, "E33.147", {"start": v(0.7, 11.33) * mm, "mid": v(0, 11.35) * mm, "end": v(-0.7, 11.33) * mm});
            skArc(sketch, "E33.148", {"start": v(8.69, -7.3) * mm, "mid": v(8.03, -8.03) * mm, "end": v(7.3, -8.69) * mm});
            skArc(sketch, "E33.150", {"start": v(-6, -9.63) * mm, "mid": v(-6.67, -9.18) * mm, "end": v(-7.3, -8.69) * mm});
            skArc(sketch, "E33.152", {"start": v(-2.74, 11.01) * mm, "mid": v(-1.78, 11.21) * mm, "end": v(-0.8, 11.32) * mm});
            skArc(sketch, "E33.153", {"start": v(6, 9.63) * mm, "mid": v(6.67, 9.18) * mm, "end": v(7.3, 8.69) * mm});
            skArc(sketch, "E33.154", {"start": v(7.3, -8.69) * mm, "mid": v(6.67, -9.18) * mm, "end": v(6, -9.63) * mm});
            skArc(sketch, "E33.155", {"start": v(-11.01, 2.74) * mm, "mid": v(-10.8, 3.5) * mm, "end": v(-10.52, 4.26) * mm});
            skArc(sketch, "E33.156", {"start": v(6, -9.63) * mm, "mid": v(5.15, -10.11) * mm, "end": v(4.26, -10.52) * mm});
            skArc(sketch, "E33.157", {"start": v(-11.32, -0.8) * mm, "mid": v(-11.35, 0) * mm, "end": v(-11.32, 0.8) * mm});
            skLineSegment(sketch, "E33.158", {"start": v(-7.3, -8.69) * mm, "end": v(-6.57, -7.68) * mm});
            skArc(sketch, "E33.159", {"start": v(11.32, -0.8) * mm, "mid": v(11.21, -1.78) * mm, "end": v(11.01, -2.74) * mm});
            skArc(sketch, "E33.160", {"start": v(9.63, 6) * mm, "mid": v(10.11, 5.15) * mm, "end": v(10.52, 4.26) * mm});
            skArc(sketch, "E33.161", {"start": v(0.8, 11.32) * mm, "mid": v(1.78, 11.21) * mm, "end": v(2.74, 11.01) * mm});
            skArc(sketch, "E33.162", {"start": v(-2.74, -11.01) * mm, "mid": v(-3.5, -10.8) * mm, "end": v(-4.26, -10.52) * mm});
            skArc(sketch, "E33.163", {"start": v(-4.26, -10.52) * mm, "mid": v(-5.15, -10.11) * mm, "end": v(-6, -9.63) * mm});
            skArc(sketch, "E33.164", {"start": v(11.01, 2.74) * mm, "mid": v(11.21, 1.78) * mm, "end": v(11.32, 0.8) * mm});
            skArc(sketch, "E33.165", {"start": v(10.52, -4.26) * mm, "mid": v(10.11, -5.15) * mm, "end": v(9.63, -6) * mm});
            skArc(sketch, "E33.167", {"start": v(4.26, -10.52) * mm, "mid": v(3.5, -10.8) * mm, "end": v(2.74, -11.01) * mm});
            skArc(sketch, "E33.168", {"start": v(-4.26, 10.52) * mm, "mid": v(-3.5, 10.8) * mm, "end": v(-2.74, 11.01) * mm});
            skArc(sketch, "E33.169", {"start": v(11.32, 0.8) * mm, "mid": v(11.35, 0) * mm, "end": v(11.32, -0.8) * mm});
            skArc(sketch, "E33.170", {"start": v(-8.69, -7.3) * mm, "mid": v(-9.18, -6.67) * mm, "end": v(-9.63, -6) * mm});
            skArc(sketch, "E33.171", {"start": v(-9.63, -6) * mm, "mid": v(-10.11, -5.15) * mm, "end": v(-10.52, -4.26) * mm});
            skArc(sketch, "E33.172", {"start": v(-9.63, 6) * mm, "mid": v(-9.18, 6.67) * mm, "end": v(-8.69, 7.3) * mm});
            skArc(sketch, "E33.173", {"start": v(11.01, -2.74) * mm, "mid": v(10.8, -3.5) * mm, "end": v(10.52, -4.26) * mm});
            skArc(sketch, "E33.174", {"start": v(-11.32, 0.8) * mm, "mid": v(-11.21, 1.78) * mm, "end": v(-11.01, 2.74) * mm});
            skArc(sketch, "E33.176", {"start": v(-7.3, -8.69) * mm, "mid": v(-8.03, -8.03) * mm, "end": v(-8.69, -7.3) * mm});
            skArc(sketch, "E33.177", {"start": v(-8.69, 7.3) * mm, "mid": v(-8.03, 8.03) * mm, "end": v(-7.3, 8.69) * mm});
            skArc(sketch, "E33.178", {"start": v(-11.01, -2.74) * mm, "mid": v(-11.21, -1.78) * mm, "end": v(-11.32, -0.8) * mm});
            skArc(sketch, "E33.179", {"start": v(2.74, -11.01) * mm, "mid": v(1.78, -11.21) * mm, "end": v(0.8, -11.32) * mm});
            skLineSegment(sketch, "E33.180", {"start": v(7.3, 8.69) * mm, "end": v(6.57, 7.68) * mm});
            skArc(sketch, "E33.181", {"start": v(7.3, 8.69) * mm, "mid": v(8.03, 8.03) * mm, "end": v(8.69, 7.3) * mm});
            skArc(sketch, "E33.182", {"start": v(-6, 9.63) * mm, "mid": v(-5.15, 10.11) * mm, "end": v(-4.26, 10.52) * mm});
            skArc(sketch, "E33.183", {"start": v(10.52, 4.26) * mm, "mid": v(10.8, 3.5) * mm, "end": v(11.01, 2.74) * mm});
            skCircle(sketch, "E33.184", {"center": v(0, 0) * mm, "radius": 7 * mm});
            skCircle(sketch, "E33.185", {"center": v(0, 0) * mm, "radius": 5.1 * mm});
            skCircle(sketch, "E33.186", {"center": v(0, 0) * mm, "radius": 3.25 * mm});
            skLineSegment(sketch, "E33.187", {"start": v(-7.3, 8.69) * mm, "end": v(-6.57, 7.68) * mm});
            skLineSegment(sketch, "E33.188", {"start": v(8.69, 7.3) * mm, "end": v(7.68, 6.57) * mm});
            skLineSegment(sketch, "E33.189", {"start": v(6, -9.63) * mm, "end": v(5.28, -8.62) * mm});
            skLineSegment(sketch, "E33.190", {"start": v(-11.32, 0.8) * mm, "end": v(-10.08, 0.8) * mm});
            skArc(sketch, "E33.191", {"start": v(9.27, 3.74) * mm, "mid": v(9.51, 3.1) * mm, "end": v(9.7, 2.42) * mm});
            skArc(sketch, "E33.193", {"start": v(-8.48, 5.3) * mm, "mid": v(-8.1, 5.88) * mm, "end": v(-7.66, 6.42) * mm});
            skLineSegment(sketch, "E33.194", {"start": v(4.26, 10.52) * mm, "end": v(3.87, 9.34) * mm});
            skLineSegment(sketch, "E33.195", {"start": v(9.63, -6) * mm, "end": v(8.62, -5.28) * mm});
            skLineSegment(sketch, "E33.196", {"start": v(7.3, 8.69) * mm, "end": v(6.57, 7.68) * mm});
            skLineSegment(sketch, "E33.197", {"start": v(4.26, -10.52) * mm, "end": v(3.87, -9.34) * mm});
            skArc(sketch, "E33.198", {"start": v(5.3, 8.48) * mm, "mid": v(5.88, 8.1) * mm, "end": v(6.42, 7.66) * mm});
            skLineSegment(sketch, "E33.199", {"start": v(10.52, 4.26) * mm, "end": v(9.34, 3.87) * mm});
            skLineSegment(sketch, "E33.201", {"start": v(-8.69, 7.3) * mm, "end": v(-7.68, 6.57) * mm});
            skLineSegment(sketch, "E33.202", {"start": v(-6, -9.63) * mm, "end": v(-5.28, -8.62) * mm});
            skLineSegment(sketch, "E33.204", {"start": v(-0.7, 9.98) * mm, "end": v(-0.7, 11.33) * mm});
            skArc(sketch, "E33.205", {"start": v(-9.7, 2.42) * mm, "mid": v(-9.51, 3.1) * mm, "end": v(-9.27, 3.74) * mm});
            skArc(sketch, "E33.206", {"start": v(-0.7, 9.98) * mm, "mid": v(0, 10) * mm, "end": v(0.7, 9.98) * mm});
            skLineSegment(sketch, "E33.207", {"start": v(-8.69, -7.3) * mm, "end": v(-7.68, -6.57) * mm});
            skArc(sketch, "E33.208", {"start": v(2.42, 9.7) * mm, "mid": v(3.1, 9.51) * mm, "end": v(3.74, 9.27) * mm});
            skLineSegment(sketch, "E33.209", {"start": v(-2.74, 11.01) * mm, "end": v(-2.35, 9.83) * mm});
            skArc(sketch, "E33.210", {"start": v(9.7, -2.42) * mm, "mid": v(9.51, -3.1) * mm, "end": v(9.27, -3.74) * mm});
            skLineSegment(sketch, "E33.211", {"start": v(-11.01, 2.74) * mm, "end": v(-9.83, 2.35) * mm});
            skArc(sketch, "E33.212", {"start": v(-3.74, 9.27) * mm, "mid": v(-3.1, 9.51) * mm, "end": v(-2.42, 9.7) * mm});
            skLineSegment(sketch, "E33.213", {"start": v(0.8, -11.32) * mm, "end": v(0.8, -10.08) * mm});
            skLineSegment(sketch, "E33.214", {"start": v(-6, 9.63) * mm, "end": v(-5.28, 8.62) * mm});
            skCircle(sketch, "E33.215", {"center": v(0, 0) * mm, "radius": 8.9 * mm});
            skLineSegment(sketch, "E33.216", {"start": v(-7.3, -8.69) * mm, "end": v(-6.57, -7.68) * mm});
            skArc(sketch, "E33.218", {"start": v(8.48, -5.3) * mm, "mid": v(8.1, -5.88) * mm, "end": v(7.66, -6.42) * mm});
            skLineSegment(sketch, "E33.219", {"start": v(9.63, 6) * mm, "end": v(8.62, 5.28) * mm});
            skLineSegment(sketch, "E33.220", {"start": v(-4.26, -10.52) * mm, "end": v(-3.87, -9.34) * mm});
            skLineSegment(sketch, "E33.221", {"start": v(-0.8, -11.32) * mm, "end": v(-0.8, -10.08) * mm});
            skArc(sketch, "E33.222", {"start": v(-9.98, -0.7) * mm, "mid": v(-10, 0) * mm, "end": v(-9.98, 0.7) * mm});
            skArc(sketch, "E33.223", {"start": v(6.42, -7.66) * mm, "mid": v(5.88, -8.1) * mm, "end": v(5.3, -8.48) * mm});
            skArc(sketch, "E33.224", {"start": v(3.74, -9.27) * mm, "mid": v(3.1, -9.51) * mm, "end": v(2.42, -9.7) * mm});
            skArc(sketch, "E33.225", {"start": v(-2.42, -9.7) * mm, "mid": v(-3.1, -9.51) * mm, "end": v(-3.74, -9.27) * mm});
            skLineSegment(sketch, "E33.226", {"start": v(0.7, 9.98) * mm, "end": v(0.7, 11.33) * mm});
            skLineSegment(sketch, "E33.227", {"start": v(-10.52, -4.26) * mm, "end": v(-9.34, -3.87) * mm});
            skLineSegment(sketch, "E33.229", {"start": v(7.3, -8.69) * mm, "end": v(6.57, -7.68) * mm});
            skArc(sketch, "E33.231", {"start": v(0.7, -9.98) * mm, "mid": v(0, -10) * mm, "end": v(-0.7, -9.98) * mm});
            skLineSegment(sketch, "E33.232", {"start": v(10.52, -4.26) * mm, "end": v(9.34, -3.87) * mm});
            skArc(sketch, "E33.233", {"start": v(-0.7, 11.33) * mm, "mid": v(-0.75, 11.33) * mm, "end": v(-0.8, 11.32) * mm});
            skLineSegment(sketch, "E33.234", {"start": v(11.32, -0.8) * mm, "end": v(10.08, -0.8) * mm});
            skLineSegment(sketch, "E33.235", {"start": v(11.01, 2.74) * mm, "end": v(9.83, 2.35) * mm});
            skArc(sketch, "E33.236", {"start": v(-7.66, -6.42) * mm, "mid": v(-8.1, -5.88) * mm, "end": v(-8.48, -5.3) * mm});
            skLineSegment(sketch, "E33.237", {"start": v(-11.01, -2.74) * mm, "end": v(-9.83, -2.35) * mm});
            skArc(sketch, "E33.238", {"start": v(0.8, 11.32) * mm, "mid": v(0.75, 11.33) * mm, "end": v(0.7, 11.33) * mm});
            skLineSegment(sketch, "E33.239", {"start": v(-9.63, -6) * mm, "end": v(-8.62, -5.28) * mm});
            skArc(sketch, "E33.240", {"start": v(9.98, 0.7) * mm, "mid": v(10, 0) * mm, "end": v(9.98, -0.7) * mm});
            skLineSegment(sketch, "E33.242", {"start": v(2.74, -11.01) * mm, "end": v(2.35, -9.83) * mm});
            skArc(sketch, "E33.243", {"start": v(-5.3, -8.48) * mm, "mid": v(-5.88, -8.1) * mm, "end": v(-6.42, -7.66) * mm});
            skLineSegment(sketch, "E33.244", {"start": v(-4.26, 10.52) * mm, "end": v(-3.87, 9.34) * mm});
            skLineSegment(sketch, "E33.245", {"start": v(8.69, -7.3) * mm, "end": v(7.68, -6.57) * mm});
            skArc(sketch, "E33.248", {"start": v(-9.27, -3.74) * mm, "mid": v(-9.51, -3.1) * mm, "end": v(-9.7, -2.42) * mm});
            skArc(sketch, "E33.249", {"start": v(-6.42, 7.66) * mm, "mid": v(-5.88, 8.1) * mm, "end": v(-5.3, 8.48) * mm});
            skLineSegment(sketch, "E33.250", {"start": v(-2.74, -11.01) * mm, "end": v(-2.35, -9.83) * mm});
            skLineSegment(sketch, "E33.251", {"start": v(6, 9.63) * mm, "end": v(5.28, 8.62) * mm});
            skArc(sketch, "E33.252", {"start": v(7.66, 6.42) * mm, "mid": v(8.1, 5.88) * mm, "end": v(8.48, 5.3) * mm});
            skArc(sketch, "E33.255", {"start": v(-0.7, 9.98) * mm, "mid": v(-0.77, 10) * mm, "end": v(-0.8, 10.08) * mm});
            skArc(sketch, "E33.256", {"start": v(8.48, -5.3) * mm, "mid": v(8.54, -5.26) * mm, "end": v(8.62, -5.28) * mm});
            skArc(sketch, "E33.257", {"start": v(-10.08, 0.8) * mm, "mid": v(-10, 0.77) * mm, "end": v(-9.98, 0.7) * mm});
            skArc(sketch, "E33.258", {"start": v(0.7, -9.98) * mm, "mid": v(0.77, -10) * mm, "end": v(0.8, -10.08) * mm});
            skArc(sketch, "E33.259", {"start": v(8.62, 5.28) * mm, "mid": v(8.54, 5.26) * mm, "end": v(8.48, 5.3) * mm});
            skArc(sketch, "E33.260", {"start": v(-6.57, -7.68) * mm, "mid": v(-6.5, -7.64) * mm, "end": v(-6.42, -7.66) * mm});
            skLineSegment(sketch, "E33.261", {"start": v(-7.3, 8.69) * mm, "end": v(-6.57, 7.68) * mm});
            skArc(sketch, "E33.262", {"start": v(-8.48, 5.3) * mm, "mid": v(-8.54, 5.26) * mm, "end": v(-8.62, 5.28) * mm});
            skLineSegment(sketch, "E33.263", {"start": v(11.32, -0.8) * mm, "end": v(10.08, -0.8) * mm});
            skLineSegment(sketch, "E33.264", {"start": v(-9.63, -6) * mm, "end": v(-8.62, -5.28) * mm});
            skLineSegment(sketch, "E33.265", {"start": v(8.69, -7.3) * mm, "end": v(7.68, -6.57) * mm});
            skArc(sketch, "E33.266", {"start": v(6.57, 7.68) * mm, "mid": v(6.5, 7.64) * mm, "end": v(6.42, 7.66) * mm});
            skLineSegment(sketch, "E33.267", {"start": v(-0.8, 10.08) * mm, "end": v(-0.8, 11.32) * mm});
            skLineSegment(sketch, "E33.268", {"start": v(2.74, 11.01) * mm, "end": v(2.35, 9.83) * mm});
            skArc(sketch, "E33.269", {"start": v(-0.8, -10.08) * mm, "mid": v(-0.77, -10) * mm, "end": v(-0.7, -9.98) * mm});
            skArc(sketch, "E33.272", {"start": v(9.83, 2.35) * mm, "mid": v(9.75, 2.36) * mm, "end": v(9.7, 2.42) * mm});
            skLineSegment(sketch, "E33.273", {"start": v(7.3, -8.69) * mm, "end": v(6.57, -7.68) * mm});
            skLineSegment(sketch, "E33.274", {"start": v(10.52, -4.26) * mm, "end": v(9.34, -3.87) * mm});
            skArc(sketch, "E33.275", {"start": v(9.34, -3.87) * mm, "mid": v(9.28, -3.82) * mm, "end": v(9.27, -3.74) * mm});
            skArc(sketch, "E33.277", {"start": v(9.27, 3.74) * mm, "mid": v(9.51, 3.1) * mm, "end": v(9.7, 2.42) * mm});
            skArc(sketch, "E33.278", {"start": v(-7.68, 6.57) * mm, "mid": v(-7.64, 6.5) * mm, "end": v(-7.66, 6.42) * mm});
            skLineSegment(sketch, "E33.279", {"start": v(-2.74, 11.01) * mm, "end": v(-2.35, 9.83) * mm});
            skArc(sketch, "E33.281", {"start": v(-8.48, 5.3) * mm, "mid": v(-8.1, 5.88) * mm, "end": v(-7.66, 6.42) * mm});
            skArc(sketch, "E33.282", {"start": v(-6.42, 7.66) * mm, "mid": v(-5.88, 8.1) * mm, "end": v(-5.3, 8.48) * mm});
            skArc(sketch, "E33.283", {"start": v(-9.83, -2.35) * mm, "mid": v(-9.75, -2.36) * mm, "end": v(-9.7, -2.42) * mm});
            skArc(sketch, "E33.285", {"start": v(-9.27, -3.74) * mm, "mid": v(-9.28, -3.82) * mm, "end": v(-9.34, -3.87) * mm});
            skLineSegment(sketch, "E33.286", {"start": v(-6, -9.63) * mm, "end": v(-5.28, -8.62) * mm});
            skLineSegment(sketch, "E33.287", {"start": v(-2.74, -11.01) * mm, "end": v(-2.35, -9.83) * mm});
            skLineSegment(sketch, "E33.289", {"start": v(4.26, -10.52) * mm, "end": v(3.87, -9.34) * mm});
            skLineSegment(sketch, "E33.290", {"start": v(-11.32, 0.8) * mm, "end": v(-10.08, 0.8) * mm});
            skLineSegment(sketch, "E33.291", {"start": v(9.63, 6) * mm, "end": v(8.62, 5.28) * mm});
            skLineSegment(sketch, "E33.292", {"start": v(-10.52, -4.26) * mm, "end": v(-9.34, -3.87) * mm});
            skLineSegment(sketch, "E33.293", {"start": v(2.74, -11.01) * mm, "end": v(2.35, -9.83) * mm});
            skLineSegment(sketch, "E33.296", {"start": v(-10.52, 4.26) * mm, "end": v(-9.34, 3.87) * mm});
            skArc(sketch, "E33.299", {"start": v(-9.7, 2.42) * mm, "mid": v(-9.75, 2.36) * mm, "end": v(-9.83, 2.35) * mm});
            skLineSegment(sketch, "E33.302", {"start": v(0.8, 10.08) * mm, "end": v(0.8, 11.32) * mm});
            skArc(sketch, "E33.306", {"start": v(-3.74, 9.27) * mm, "mid": v(-3.82, 9.28) * mm, "end": v(-3.87, 9.34) * mm});
            skArc(sketch, "E33.307", {"start": v(-5.3, -8.48) * mm, "mid": v(-5.88, -8.1) * mm, "end": v(-6.42, -7.66) * mm});
            skArc(sketch, "E33.309", {"start": v(9.7, -2.42) * mm, "mid": v(9.75, -2.36) * mm, "end": v(9.83, -2.35) * mm});
            skLineSegment(sketch, "E33.311", {"start": v(-6, 9.63) * mm, "end": v(-5.28, 8.62) * mm});
            skLineSegment(sketch, "E33.313", {"start": v(-11.01, -2.74) * mm, "end": v(-9.83, -2.35) * mm});
            skArc(sketch, "E33.318", {"start": v(6.42, -7.66) * mm, "mid": v(6.5, -7.64) * mm, "end": v(6.57, -7.68) * mm});
            skArc(sketch, "E33.319", {"start": v(-9.98, -0.7) * mm, "mid": v(-10, -0.77) * mm, "end": v(-10.08, -0.8) * mm});
            skArc(sketch, "E33.320", {"start": v(2.42, 9.7) * mm, "mid": v(2.36, 9.75) * mm, "end": v(2.35, 9.83) * mm});
            skArc(sketch, "E33.322", {"start": v(-2.42, -9.7) * mm, "mid": v(-3.1, -9.51) * mm, "end": v(-3.74, -9.27) * mm});
            skLineSegment(sketch, "E33.323", {"start": v(-4.26, 10.52) * mm, "end": v(-3.87, 9.34) * mm});
            skArc(sketch, "E33.326", {"start": v(7.68, -6.57) * mm, "mid": v(7.64, -6.5) * mm, "end": v(7.66, -6.42) * mm});
            skLineSegment(sketch, "E33.327", {"start": v(-9.63, 6) * mm, "end": v(-8.62, 5.28) * mm});
            skArc(sketch, "E33.328", {"start": v(-5.3, -8.48) * mm, "mid": v(-5.26, -8.54) * mm, "end": v(-5.28, -8.62) * mm});
            skArc(sketch, "E33.329", {"start": v(-2.35, 9.83) * mm, "mid": v(-2.36, 9.75) * mm, "end": v(-2.42, 9.7) * mm});
            skArc(sketch, "E33.330", {"start": v(-6.42, 7.66) * mm, "mid": v(-6.5, 7.64) * mm, "end": v(-6.57, 7.68) * mm});
            skArc(sketch, "E33.331", {"start": v(-2.42, -9.7) * mm, "mid": v(-2.36, -9.75) * mm, "end": v(-2.35, -9.83) * mm});
            skLineSegment(sketch, "E33.332", {"start": v(-0.8, -11.32) * mm, "end": v(-0.8, -10.08) * mm});
            skLineSegment(sketch, "E33.334", {"start": v(-11.32, -0.8) * mm, "end": v(-10.08, -0.8) * mm});
            skArc(sketch, "E33.335", {"start": v(-3.87, -9.34) * mm, "mid": v(-3.82, -9.28) * mm, "end": v(-3.74, -9.27) * mm});
            skLineSegment(sketch, "E33.336", {"start": v(11.01, 2.74) * mm, "end": v(9.83, 2.35) * mm});
            skArc(sketch, "E33.337", {"start": v(-7.66, -6.42) * mm, "mid": v(-7.64, -6.5) * mm, "end": v(-7.68, -6.57) * mm});
            skLineSegment(sketch, "E33.340", {"start": v(11.01, -2.74) * mm, "end": v(9.83, -2.35) * mm});
            skArc(sketch, "E33.342", {"start": v(-8.62, -5.28) * mm, "mid": v(-8.54, -5.26) * mm, "end": v(-8.48, -5.3) * mm});
            skArc(sketch, "E33.343", {"start": v(-9.7, 2.42) * mm, "mid": v(-9.51, 3.1) * mm, "end": v(-9.27, 3.74) * mm});
            skLineSegment(sketch, "E33.344", {"start": v(9.63, -6) * mm, "end": v(8.62, -5.28) * mm});
            skArc(sketch, "E33.345", {"start": v(0.7, -9.98) * mm, "mid": v(0, -10) * mm, "end": v(-0.7, -9.98) * mm});
            skArc(sketch, "E33.346", {"start": v(7.66, 6.42) * mm, "mid": v(7.64, 6.5) * mm, "end": v(7.68, 6.57) * mm});
            skArc(sketch, "E33.349", {"start": v(5.3, 8.48) * mm, "mid": v(5.26, 8.54) * mm, "end": v(5.28, 8.62) * mm});
            skArc(sketch, "E33.350", {"start": v(8.48, -5.3) * mm, "mid": v(8.1, -5.88) * mm, "end": v(7.66, -6.42) * mm});
            skArc(sketch, "E33.351", {"start": v(10.08, -0.8) * mm, "mid": v(10, -0.77) * mm, "end": v(9.98, -0.7) * mm});
            skLineSegment(sketch, "E33.353", {"start": v(10.52, 4.26) * mm, "end": v(9.34, 3.87) * mm});
            skLineSegment(sketch, "E33.355", {"start": v(11.32, 0.8) * mm, "end": v(10.08, 0.8) * mm});
            skArc(sketch, "E33.356", {"start": v(9.27, 3.74) * mm, "mid": v(9.28, 3.82) * mm, "end": v(9.34, 3.87) * mm});
            skLineSegment(sketch, "E33.357", {"start": v(4.26, 10.52) * mm, "end": v(3.87, 9.34) * mm});
            skArc(sketch, "E33.358", {"start": v(3.87, 9.34) * mm, "mid": v(3.82, 9.28) * mm, "end": v(3.74, 9.27) * mm});
            skArc(sketch, "E33.359", {"start": v(-5.28, 8.62) * mm, "mid": v(-5.26, 8.54) * mm, "end": v(-5.3, 8.48) * mm});
            skLineSegment(sketch, "E33.362", {"start": v(-11.01, 2.74) * mm, "end": v(-9.83, 2.35) * mm});
            skArc(sketch, "E33.363", {"start": v(-9.34, 3.87) * mm, "mid": v(-9.28, 3.82) * mm, "end": v(-9.27, 3.74) * mm});
            skArc(sketch, "E33.365", {"start": v(5.28, -8.62) * mm, "mid": v(5.26, -8.54) * mm, "end": v(5.3, -8.48) * mm});
            skArc(sketch, "E33.366", {"start": v(6.42, -7.66) * mm, "mid": v(5.88, -8.1) * mm, "end": v(5.3, -8.48) * mm});
            skLineSegment(sketch, "E33.370", {"start": v(-8.69, -7.3) * mm, "end": v(-7.68, -6.57) * mm});
            skArc(sketch, "E33.371", {"start": v(9.98, 0.7) * mm, "mid": v(10, 0.77) * mm, "end": v(10.08, 0.8) * mm});
            skLineSegment(sketch, "E33.372", {"start": v(0.8, -11.32) * mm, "end": v(0.8, -10.08) * mm});
            skLineSegment(sketch, "E33.373", {"start": v(8.69, 7.3) * mm, "end": v(7.68, 6.57) * mm});
            skArc(sketch, "E33.375", {"start": v(3.74, -9.27) * mm, "mid": v(3.82, -9.28) * mm, "end": v(3.87, -9.34) * mm});
            skArc(sketch, "E33.382", {"start": v(9.98, 0.7) * mm, "mid": v(10, 0) * mm, "end": v(9.98, -0.7) * mm});
            skLineSegment(sketch, "E33.386", {"start": v(11.32, 0.8) * mm, "end": v(10.08, 0.8) * mm});
            skArc(sketch, "E33.389", {"start": v(-9.27, -3.74) * mm, "mid": v(-9.51, -3.1) * mm, "end": v(-9.7, -2.42) * mm});
            skArc(sketch, "E33.395", {"start": v(2.35, -9.83) * mm, "mid": v(2.36, -9.75) * mm, "end": v(2.42, -9.7) * mm});
            skArc(sketch, "E33.396", {"start": v(-7.66, -6.42) * mm, "mid": v(-8.1, -5.88) * mm, "end": v(-8.48, -5.3) * mm});
            skArc(sketch, "E33.405", {"start": v(-3.74, 9.27) * mm, "mid": v(-3.1, 9.51) * mm, "end": v(-2.42, 9.7) * mm});
            skLineSegment(sketch, "E33.406", {"start": v(11.01, -2.74) * mm, "end": v(9.83, -2.35) * mm});
            skLineSegment(sketch, "E33.413", {"start": v(-11.32, -0.8) * mm, "end": v(-10.08, -0.8) * mm});
            skLineSegment(sketch, "E33.414", {"start": v(-10.52, 4.26) * mm, "end": v(-9.34, 3.87) * mm});
            skArc(sketch, "E33.416", {"start": v(-0.8, 10.08) * mm, "mid": v(-0.77, 10) * mm, "end": v(-0.7, 9.98) * mm});
            skArc(sketch, "E33.417", {"start": v(2.42, 9.7) * mm, "mid": v(3.1, 9.51) * mm, "end": v(3.74, 9.27) * mm});
            skArc(sketch, "E33.419", {"start": v(-9.98, -0.7) * mm, "mid": v(-10, 0) * mm, "end": v(-9.98, 0.7) * mm});
            skArc(sketch, "E33.421", {"start": v(9.7, -2.42) * mm, "mid": v(9.51, -3.1) * mm, "end": v(9.27, -3.74) * mm});
            skLineSegment(sketch, "E33.422", {"start": v(2.74, 11.01) * mm, "end": v(2.35, 9.83) * mm});
            skLineSegment(sketch, "E33.427", {"start": v(0.8, 10.08) * mm, "end": v(0.8, 11.32) * mm});
            skArc(sketch, "E33.435", {"start": v(3.74, -9.27) * mm, "mid": v(3.1, -9.51) * mm, "end": v(2.42, -9.7) * mm});
            skLineSegment(sketch, "E33.436", {"start": v(-9.63, 6) * mm, "end": v(-8.62, 5.28) * mm});
            skArc(sketch, "E33.437", {"start": v(5.3, 8.48) * mm, "mid": v(5.88, 8.1) * mm, "end": v(6.42, 7.66) * mm});
            skArc(sketch, "E33.438", {"start": v(7.66, 6.42) * mm, "mid": v(8.1, 5.88) * mm, "end": v(8.48, 5.3) * mm});
            skArc(sketch, "E33.442", {"start": v(0.8, 10.08) * mm, "mid": v(0.77, 10) * mm, "end": v(0.7, 9.98) * mm});
            skArc(sketch, "E33.443", {"start": v(-6.57, -7.68) * mm, "mid": v(-6.5, -7.64) * mm, "end": v(-6.42, -7.66) * mm});
            skArc(sketch, "E33.444", {"start": v(8.48, -5.3) * mm, "mid": v(8.54, -5.26) * mm, "end": v(8.62, -5.28) * mm});
            skArc(sketch, "E33.445", {"start": v(7.66, 6.42) * mm, "mid": v(7.64, 6.5) * mm, "end": v(7.68, 6.57) * mm});
            skArc(sketch, "E33.446", {"start": v(9.27, 3.74) * mm, "mid": v(9.28, 3.82) * mm, "end": v(9.34, 3.87) * mm});
            skArc(sketch, "E33.447", {"start": v(2.42, 9.7) * mm, "mid": v(2.36, 9.75) * mm, "end": v(2.35, 9.83) * mm});
            skArc(sketch, "E33.448", {"start": v(-10.08, 0.8) * mm, "mid": v(-10, 0.77) * mm, "end": v(-9.98, 0.7) * mm});
            skArc(sketch, "E33.449", {"start": v(-7.68, 6.57) * mm, "mid": v(-7.64, 6.5) * mm, "end": v(-7.66, 6.42) * mm});
            skArc(sketch, "E33.450", {"start": v(9.34, -3.87) * mm, "mid": v(9.28, -3.82) * mm, "end": v(9.27, -3.74) * mm});
            skArc(sketch, "E33.451", {"start": v(-0.8, -10.08) * mm, "mid": v(-0.77, -10) * mm, "end": v(-0.7, -9.98) * mm});
            skArc(sketch, "E33.452", {"start": v(10.08, -0.8) * mm, "mid": v(10, -0.77) * mm, "end": v(9.98, -0.7) * mm});
            skArc(sketch, "E33.453", {"start": v(8.62, 5.28) * mm, "mid": v(8.54, 5.26) * mm, "end": v(8.48, 5.3) * mm});
            skArc(sketch, "E33.455", {"start": v(7.68, -6.57) * mm, "mid": v(7.64, -6.5) * mm, "end": v(7.66, -6.42) * mm});
            skArc(sketch, "E33.457", {"start": v(3.74, -9.27) * mm, "mid": v(3.82, -9.28) * mm, "end": v(3.87, -9.34) * mm});
            skArc(sketch, "E33.461", {"start": v(6.42, -7.66) * mm, "mid": v(6.5, -7.64) * mm, "end": v(6.57, -7.68) * mm});
            skArc(sketch, "E33.462", {"start": v(-2.42, -9.7) * mm, "mid": v(-2.36, -9.75) * mm, "end": v(-2.35, -9.83) * mm});
            skArc(sketch, "E33.463", {"start": v(-8.48, 5.3) * mm, "mid": v(-8.54, 5.26) * mm, "end": v(-8.62, 5.28) * mm});
            skArc(sketch, "E33.464", {"start": v(9.83, 2.35) * mm, "mid": v(9.75, 2.36) * mm, "end": v(9.7, 2.42) * mm});
            skArc(sketch, "E33.465", {"start": v(3.87, 9.34) * mm, "mid": v(3.82, 9.28) * mm, "end": v(3.74, 9.27) * mm});
            skArc(sketch, "E33.466", {"start": v(-2.35, 9.83) * mm, "mid": v(-2.36, 9.75) * mm, "end": v(-2.42, 9.7) * mm});
            skArc(sketch, "E33.467", {"start": v(-8.62, -5.28) * mm, "mid": v(-8.54, -5.26) * mm, "end": v(-8.48, -5.3) * mm});
            skLineSegment(sketch, "E33.470", {"start": v(-0.8, 11.32) * mm, "end": v(-0.8, 10.08) * mm});
            skArc(sketch, "E33.471", {"start": v(0.7, -9.98) * mm, "mid": v(0.77, -10) * mm, "end": v(0.8, -10.08) * mm});
            skArc(sketch, "E33.472", {"start": v(-3.87, -9.34) * mm, "mid": v(-3.82, -9.28) * mm, "end": v(-3.74, -9.27) * mm});
            skArc(sketch, "E33.473", {"start": v(-9.98, -0.7) * mm, "mid": v(-10, -0.77) * mm, "end": v(-10.08, -0.8) * mm});
            skArc(sketch, "E33.474", {"start": v(6.57, 7.68) * mm, "mid": v(6.5, 7.64) * mm, "end": v(6.42, 7.66) * mm});
            skArc(sketch, "E33.477", {"start": v(9.7, -2.42) * mm, "mid": v(9.75, -2.36) * mm, "end": v(9.83, -2.35) * mm});
            skArc(sketch, "E33.478", {"start": v(-9.34, 3.87) * mm, "mid": v(-9.28, 3.82) * mm, "end": v(-9.27, 3.74) * mm});
            skArc(sketch, "E33.480", {"start": v(9.98, 0.7) * mm, "mid": v(10, 0.77) * mm, "end": v(10.08, 0.8) * mm});
            skArc(sketch, "E33.481", {"start": v(-3.74, 9.27) * mm, "mid": v(-3.82, 9.28) * mm, "end": v(-3.87, 9.34) * mm});
            skArc(sketch, "E33.482", {"start": v(-6.42, 7.66) * mm, "mid": v(-6.5, 7.64) * mm, "end": v(-6.57, 7.68) * mm});
            skArc(sketch, "E33.483", {"start": v(2.35, -9.83) * mm, "mid": v(2.36, -9.75) * mm, "end": v(2.42, -9.7) * mm});
            skArc(sketch, "E33.488", {"start": v(-9.27, -3.74) * mm, "mid": v(-9.28, -3.82) * mm, "end": v(-9.34, -3.87) * mm});
            skArc(sketch, "E33.491", {"start": v(-7.66, -6.42) * mm, "mid": v(-7.64, -6.5) * mm, "end": v(-7.68, -6.57) * mm});
            skArc(sketch, "E33.493", {"start": v(-5.28, 8.62) * mm, "mid": v(-5.26, 8.54) * mm, "end": v(-5.3, 8.48) * mm});
            skArc(sketch, "E33.494", {"start": v(-9.7, 2.42) * mm, "mid": v(-9.75, 2.36) * mm, "end": v(-9.83, 2.35) * mm});
            skArc(sketch, "E33.495", {"start": v(8.48, -5.3) * mm, "mid": v(8.54, -5.26) * mm, "end": v(8.62, -5.28) * mm});
            skArc(sketch, "E33.496", {"start": v(8.62, 5.28) * mm, "mid": v(8.54, 5.26) * mm, "end": v(8.48, 5.3) * mm});
            skArc(sketch, "E33.497", {"start": v(-10.08, 0.8) * mm, "mid": v(-10, 0.77) * mm, "end": v(-9.98, 0.7) * mm});
            skArc(sketch, "E33.498", {"start": v(0.7, -9.98) * mm, "mid": v(0.77, -10) * mm, "end": v(0.8, -10.08) * mm});
            skArc(sketch, "E33.499", {"start": v(-5.3, -8.48) * mm, "mid": v(-5.26, -8.54) * mm, "end": v(-5.28, -8.62) * mm});
            skArc(sketch, "E33.500", {"start": v(5.28, -8.62) * mm, "mid": v(5.26, -8.54) * mm, "end": v(5.3, -8.48) * mm});
            skArc(sketch, "E33.501", {"start": v(0.7, 9.98) * mm, "mid": v(0.77, 10) * mm, "end": v(0.8, 10.08) * mm});
            skArc(sketch, "E33.502", {"start": v(-9.83, -2.35) * mm, "mid": v(-9.75, -2.36) * mm, "end": v(-9.7, -2.42) * mm});
            skArc(sketch, "E33.503", {"start": v(5.3, 8.48) * mm, "mid": v(5.26, 8.54) * mm, "end": v(5.28, 8.62) * mm});
            skArc(sketch, "E33.504", {"start": v(-6.57, -7.68) * mm, "mid": v(-6.5, -7.64) * mm, "end": v(-6.42, -7.66) * mm});
            skSolve(sketch);
        }
        {
            var Q0;
            {var subQ0=sQuery(id+"F21.wireOp",EDGE,"E33.261");var subQ1=sQuery(id+"F21.wireOp",EDGE,"E33.107");var subQ2=makeQuery(id+"F21.imprint","INTERSECT",VERTEX,{"derivedFrom":[subQ1,subQ0]});Q0=makeQuery(id+"F21.imprint","IMPRINT",FACE,{"disambiguationData":[TD([[makeQuery(id+"F21.imprint","IMPRINT",EDGE,{"disambiguationData":[TD([[subQ2,-1.0]])],"derivedFrom":subQ1}),-1.0]])]});}
            var Q1;
            Q1=makeQuery(id+"F21.imprint","IMPRINT",FACE,{"disambiguationData":[TD([[makeQuery(id+"F21.imprint","IMPRINT",EDGE,{"derivedFrom":sQuery(id+"F21.wireOp",EDGE,"E33.282")}),1.0]])]});
            var Q2;
            {var subQ0=sQuery(id+"F21.wireOp",EDGE,"E33.279");var subQ1=sQuery(id+"F21.wireOp",EDGE,"E33.107");var subQ2=makeQuery(id+"F21.imprint","INTERSECT",VERTEX,{"derivedFrom":[subQ1,subQ0]});Q2=makeQuery(id+"F21.imprint","IMPRINT",FACE,{"disambiguationData":[TD([[makeQuery(id+"F21.imprint","IMPRINT",EDGE,{"disambiguationData":[TD([[subQ2,1.0]])],"derivedFrom":subQ1}),-1.0]])]});}
            var Q3;
            Q3=makeQuery(id+"F21.imprint","IMPRINT",FACE,{"disambiguationData":[TD([[makeQuery(id+"F21.imprint","IMPRINT",EDGE,{"derivedFrom":sQuery(id+"F21.wireOp",EDGE,"E33.405")}),1.0]])]});
            var Q4;
            {var subQ0=sQuery(id+"F21.wireOp",EDGE,"E33.107");var subQ1=sQuery(id+"F21.wireOp",EDGE,"E33.83");var subQ2=makeQuery(id+"F21.imprint","INTERSECT",VERTEX,{"derivedFrom":[subQ1,subQ0]});Q4=makeQuery(id+"F21.imprint","IMPRINT",FACE,{"disambiguationData":[TD([[makeQuery(id+"F21.imprint","IMPRINT",EDGE,{"disambiguationData":[TD([[subQ2,1.0]])],"derivedFrom":subQ1}),1.0]])]});}
            var Q5;
            {var subQ0=sQuery(id+"F21.wireOp",EDGE,"E33.107");var subQ1=sQuery(id+"F21.wireOp",EDGE,"E33.83");var subQ2=makeQuery(id+"F21.imprint","INTERSECT",VERTEX,{"derivedFrom":[subQ1,subQ0]});Q5=makeQuery(id+"F21.imprint","IMPRINT",FACE,{"disambiguationData":[TD([[makeQuery(id+"F21.imprint","IMPRINT",EDGE,{"disambiguationData":[TD([[subQ2,1.0]])],"derivedFrom":subQ1}),-1.0]])]});}
            var Q6;
            {var subQ0=sQuery(id+"F21.wireOp",EDGE,"E33.206");var subQ1=sQuery(id+"F21.wireOp",EDGE,"E33.83");var subQ2=makeQuery(id+"F21.imprint","INTERSECT",VERTEX,{"derivedFrom":[subQ1,subQ0]});Q6=makeQuery(id+"F21.imprint","IMPRINT",FACE,{"disambiguationData":[TD([[makeQuery(id+"F21.imprint","IMPRINT",EDGE,{"disambiguationData":[TD([[subQ2,-1.0]])],"derivedFrom":subQ1}),1.0]])]});}
            var Q7;
            {var subQ0=sQuery(id+"F21.wireOp",EDGE,"E33.206");var subQ1=sQuery(id+"F21.wireOp",EDGE,"E33.83");var subQ2=makeQuery(id+"F21.imprint","INTERSECT",VERTEX,{"derivedFrom":[subQ1,subQ0]});Q7=makeQuery(id+"F21.imprint","IMPRINT",FACE,{"disambiguationData":[TD([[makeQuery(id+"F21.imprint","IMPRINT",EDGE,{"disambiguationData":[TD([[subQ2,-1.0]])],"derivedFrom":subQ1}),-1.0]])]});}
            var Q8;
            {var subQ0=sQuery(id+"F21.wireOp",EDGE,"E33.357");var subQ1=sQuery(id+"F21.wireOp",EDGE,"E33.107");var subQ2=makeQuery(id+"F21.imprint","INTERSECT",VERTEX,{"derivedFrom":[subQ1,subQ0]});Q8=makeQuery(id+"F21.imprint","IMPRINT",FACE,{"disambiguationData":[TD([[makeQuery(id+"F21.imprint","IMPRINT",EDGE,{"disambiguationData":[TD([[subQ2,1.0]])],"derivedFrom":subQ1}),-1.0]])]});}
            var Q9;
            Q9=makeQuery(id+"F21.imprint","IMPRINT",FACE,{"disambiguationData":[TD([[makeQuery(id+"F21.imprint","IMPRINT",EDGE,{"derivedFrom":sQuery(id+"F21.wireOp",EDGE,"E33.417")}),1.0]])]});
            var Q10;
            {var subQ0=sQuery(id+"F21.wireOp",EDGE,"E33.196");var subQ1=sQuery(id+"F21.wireOp",EDGE,"E33.107");var subQ2=makeQuery(id+"F21.imprint","INTERSECT",VERTEX,{"derivedFrom":[subQ1,subQ0]});Q10=makeQuery(id+"F21.imprint","IMPRINT",FACE,{"disambiguationData":[TD([[makeQuery(id+"F21.imprint","IMPRINT",EDGE,{"disambiguationData":[TD([[subQ2,1.0]])],"derivedFrom":subQ1}),-1.0]])]});}
            var Q11;
            Q11=makeQuery(id+"F21.imprint","IMPRINT",FACE,{"disambiguationData":[TD([[makeQuery(id+"F21.imprint","IMPRINT",EDGE,{"derivedFrom":sQuery(id+"F21.wireOp",EDGE,"E33.437")}),1.0]])]});
            var Q12;
            {var subQ0=sQuery(id+"F21.wireOp",EDGE,"E33.291");var subQ1=sQuery(id+"F21.wireOp",EDGE,"E33.107");var subQ2=makeQuery(id+"F21.imprint","INTERSECT",VERTEX,{"derivedFrom":[subQ1,subQ0]});Q12=makeQuery(id+"F21.imprint","IMPRINT",FACE,{"disambiguationData":[TD([[makeQuery(id+"F21.imprint","IMPRINT",EDGE,{"disambiguationData":[TD([[subQ2,1.0]])],"derivedFrom":subQ1}),-1.0]])]});}
            var Q13;
            Q13=makeQuery(id+"F21.imprint","IMPRINT",FACE,{"disambiguationData":[TD([[makeQuery(id+"F21.imprint","IMPRINT",EDGE,{"derivedFrom":sQuery(id+"F21.wireOp",EDGE,"E33.438")}),1.0]])]});
            var Q14;
            {var subQ0=sQuery(id+"F21.wireOp",EDGE,"E33.336");var subQ1=sQuery(id+"F21.wireOp",EDGE,"E33.107");var subQ2=makeQuery(id+"F21.imprint","INTERSECT",VERTEX,{"derivedFrom":[subQ1,subQ0]});Q14=makeQuery(id+"F21.imprint","IMPRINT",FACE,{"disambiguationData":[TD([[makeQuery(id+"F21.imprint","IMPRINT",EDGE,{"disambiguationData":[TD([[subQ2,1.0]])],"derivedFrom":subQ1}),-1.0]])]});}
            var Q15;
            Q15=makeQuery(id+"F21.imprint","IMPRINT",FACE,{"disambiguationData":[TD([[makeQuery(id+"F21.imprint","IMPRINT",EDGE,{"derivedFrom":sQuery(id+"F21.wireOp",EDGE,"E33.277")}),1.0]])]});
            var Q16;
            Q16=makeQuery(id+"F21.imprint","IMPRINT",FACE,{"disambiguationData":[TD([[makeQuery(id+"F21.imprint","IMPRINT",EDGE,{"derivedFrom":sQuery(id+"F21.wireOp",EDGE,"E33.382")}),1.0]])]});
            var Q17;
            {var subQ0=sQuery(id+"F21.wireOp",EDGE,"E33.263");var subQ1=sQuery(id+"F21.wireOp",EDGE,"E33.107");var subQ2=makeQuery(id+"F21.imprint","INTERSECT",VERTEX,{"derivedFrom":[subQ1,subQ0]});Q17=makeQuery(id+"F21.imprint","IMPRINT",FACE,{"disambiguationData":[TD([[makeQuery(id+"F21.imprint","IMPRINT",EDGE,{"disambiguationData":[TD([[subQ2,1.0]])],"derivedFrom":subQ1}),-1.0]])]});}
            var Q18;
            Q18=makeQuery(id+"F21.imprint","IMPRINT",FACE,{"disambiguationData":[TD([[makeQuery(id+"F21.imprint","IMPRINT",EDGE,{"derivedFrom":sQuery(id+"F21.wireOp",EDGE,"E33.421")}),1.0]])]});
            var Q19;
            {var subQ0=sQuery(id+"F21.wireOp",EDGE,"E33.274");var subQ1=sQuery(id+"F21.wireOp",EDGE,"E33.107");var subQ2=makeQuery(id+"F21.imprint","INTERSECT",VERTEX,{"derivedFrom":[subQ1,subQ0]});Q19=makeQuery(id+"F21.imprint","IMPRINT",FACE,{"disambiguationData":[TD([[makeQuery(id+"F21.imprint","IMPRINT",EDGE,{"disambiguationData":[TD([[subQ2,1.0]])],"derivedFrom":subQ1}),-1.0]])]});}
            var Q20;
            Q20=makeQuery(id+"F21.imprint","IMPRINT",FACE,{"disambiguationData":[TD([[makeQuery(id+"F21.imprint","IMPRINT",EDGE,{"derivedFrom":sQuery(id+"F21.wireOp",EDGE,"E33.350")}),1.0]])]});
            var Q21;
            {var subQ0=sQuery(id+"F21.wireOp",EDGE,"E33.265");var subQ1=sQuery(id+"F21.wireOp",EDGE,"E33.107");var subQ2=makeQuery(id+"F21.imprint","INTERSECT",VERTEX,{"derivedFrom":[subQ1,subQ0]});Q21=makeQuery(id+"F21.imprint","IMPRINT",FACE,{"disambiguationData":[TD([[makeQuery(id+"F21.imprint","IMPRINT",EDGE,{"disambiguationData":[TD([[subQ2,1.0]])],"derivedFrom":subQ1}),-1.0]])]});}
            var Q22;
            Q22=makeQuery(id+"F21.imprint","IMPRINT",FACE,{"disambiguationData":[TD([[makeQuery(id+"F21.imprint","IMPRINT",EDGE,{"derivedFrom":sQuery(id+"F21.wireOp",EDGE,"E33.366")}),1.0]])]});
            var Q23;
            {var subQ0=sQuery(id+"F21.wireOp",EDGE,"E33.189");var subQ1=sQuery(id+"F21.wireOp",EDGE,"E33.107");var subQ2=makeQuery(id+"F21.imprint","INTERSECT",VERTEX,{"derivedFrom":[subQ1,subQ0]});Q23=makeQuery(id+"F21.imprint","IMPRINT",FACE,{"disambiguationData":[TD([[makeQuery(id+"F21.imprint","IMPRINT",EDGE,{"disambiguationData":[TD([[subQ2,1.0]])],"derivedFrom":subQ1}),-1.0]])]});}
            var Q24;
            Q24=makeQuery(id+"F21.imprint","IMPRINT",FACE,{"disambiguationData":[TD([[makeQuery(id+"F21.imprint","IMPRINT",EDGE,{"derivedFrom":sQuery(id+"F21.wireOp",EDGE,"E33.435")}),1.0]])]});
            var Q25;
            {var subQ0=sQuery(id+"F21.wireOp",EDGE,"E33.289");var subQ1=sQuery(id+"F21.wireOp",EDGE,"E33.107");var subQ2=makeQuery(id+"F21.imprint","INTERSECT",VERTEX,{"derivedFrom":[subQ1,subQ0]});Q25=makeQuery(id+"F21.imprint","IMPRINT",FACE,{"disambiguationData":[TD([[makeQuery(id+"F21.imprint","IMPRINT",EDGE,{"disambiguationData":[TD([[subQ2,-1.0]])],"derivedFrom":subQ1}),-1.0]])]});}
            var Q26;
            Q26=makeQuery(id+"F21.imprint","IMPRINT",FACE,{"disambiguationData":[TD([[makeQuery(id+"F21.imprint","IMPRINT",EDGE,{"derivedFrom":sQuery(id+"F21.wireOp",EDGE,"E33.345")}),1.0]])]});
            var Q27;
            {var subQ0=sQuery(id+"F21.wireOp",EDGE,"E33.332");var subQ1=sQuery(id+"F21.wireOp",EDGE,"E33.107");var subQ2=makeQuery(id+"F21.imprint","INTERSECT",VERTEX,{"derivedFrom":[subQ1,subQ0]});Q27=makeQuery(id+"F21.imprint","IMPRINT",FACE,{"disambiguationData":[TD([[makeQuery(id+"F21.imprint","IMPRINT",EDGE,{"disambiguationData":[TD([[subQ2,1.0]])],"derivedFrom":subQ1}),-1.0]])]});}
            var Q28;
            Q28=makeQuery(id+"F21.imprint","IMPRINT",FACE,{"disambiguationData":[TD([[makeQuery(id+"F21.imprint","IMPRINT",EDGE,{"derivedFrom":sQuery(id+"F21.wireOp",EDGE,"E33.322")}),1.0]])]});
            var Q29;
            {var subQ0=sQuery(id+"F21.wireOp",EDGE,"E33.220");var subQ1=sQuery(id+"F21.wireOp",EDGE,"E33.107");var subQ2=makeQuery(id+"F21.imprint","INTERSECT",VERTEX,{"derivedFrom":[subQ1,subQ0]});Q29=makeQuery(id+"F21.imprint","IMPRINT",FACE,{"disambiguationData":[TD([[makeQuery(id+"F21.imprint","IMPRINT",EDGE,{"disambiguationData":[TD([[subQ2,1.0]])],"derivedFrom":subQ1}),-1.0]])]});}
            var Q30;
            Q30=makeQuery(id+"F21.imprint","IMPRINT",FACE,{"disambiguationData":[TD([[makeQuery(id+"F21.imprint","IMPRINT",EDGE,{"derivedFrom":sQuery(id+"F21.wireOp",EDGE,"E33.307")}),1.0]])]});
            var Q31;
            {var subQ0=sQuery(id+"F21.wireOp",EDGE,"E33.216");var subQ1=sQuery(id+"F21.wireOp",EDGE,"E33.107");var subQ2=makeQuery(id+"F21.imprint","INTERSECT",VERTEX,{"derivedFrom":[subQ1,subQ0]});Q31=makeQuery(id+"F21.imprint","IMPRINT",FACE,{"disambiguationData":[TD([[makeQuery(id+"F21.imprint","IMPRINT",EDGE,{"disambiguationData":[TD([[subQ2,1.0]])],"derivedFrom":subQ1}),-1.0]])]});}
            var Q32;
            Q32=makeQuery(id+"F21.imprint","IMPRINT",FACE,{"disambiguationData":[TD([[makeQuery(id+"F21.imprint","IMPRINT",EDGE,{"derivedFrom":sQuery(id+"F21.wireOp",EDGE,"E33.396")}),1.0]])]});
            var Q33;
            {var subQ0=sQuery(id+"F21.wireOp",EDGE,"E33.264");var subQ1=sQuery(id+"F21.wireOp",EDGE,"E33.107");var subQ2=makeQuery(id+"F21.imprint","INTERSECT",VERTEX,{"derivedFrom":[subQ1,subQ0]});Q33=makeQuery(id+"F21.imprint","IMPRINT",FACE,{"disambiguationData":[TD([[makeQuery(id+"F21.imprint","IMPRINT",EDGE,{"disambiguationData":[TD([[subQ2,1.0]])],"derivedFrom":subQ1}),-1.0]])]});}
            var Q34;
            Q34=makeQuery(id+"F21.imprint","IMPRINT",FACE,{"disambiguationData":[TD([[makeQuery(id+"F21.imprint","IMPRINT",EDGE,{"derivedFrom":sQuery(id+"F21.wireOp",EDGE,"E33.389")}),1.0]])]});
            var Q35;
            {var subQ0=sQuery(id+"F21.wireOp",EDGE,"E33.292");var subQ1=sQuery(id+"F21.wireOp",EDGE,"E33.107");var subQ2=makeQuery(id+"F21.imprint","INTERSECT",VERTEX,{"derivedFrom":[subQ1,subQ0]});Q35=makeQuery(id+"F21.imprint","IMPRINT",FACE,{"disambiguationData":[TD([[makeQuery(id+"F21.imprint","IMPRINT",EDGE,{"disambiguationData":[TD([[subQ2,-1.0]])],"derivedFrom":subQ1}),-1.0]])]});}
            var Q36;
            Q36=makeQuery(id+"F21.imprint","IMPRINT",FACE,{"disambiguationData":[TD([[makeQuery(id+"F21.imprint","IMPRINT",EDGE,{"derivedFrom":sQuery(id+"F21.wireOp",EDGE,"E33.419")}),1.0]])]});
            var Q37;
            {var subQ0=sQuery(id+"F21.wireOp",EDGE,"E33.290");var subQ1=sQuery(id+"F21.wireOp",EDGE,"E33.107");var subQ2=makeQuery(id+"F21.imprint","INTERSECT",VERTEX,{"derivedFrom":[subQ1,subQ0]});Q37=makeQuery(id+"F21.imprint","IMPRINT",FACE,{"disambiguationData":[TD([[makeQuery(id+"F21.imprint","IMPRINT",EDGE,{"disambiguationData":[TD([[subQ2,1.0]])],"derivedFrom":subQ1}),-1.0]])]});}
            var Q38;
            Q38=makeQuery(id+"F21.imprint","IMPRINT",FACE,{"disambiguationData":[TD([[makeQuery(id+"F21.imprint","IMPRINT",EDGE,{"derivedFrom":sQuery(id+"F21.wireOp",EDGE,"E33.343")}),1.0]])]});
            var Q39;
            {var subQ0=sQuery(id+"F21.wireOp",EDGE,"E33.362");var subQ1=sQuery(id+"F21.wireOp",EDGE,"E33.107");var subQ2=makeQuery(id+"F21.imprint","INTERSECT",VERTEX,{"derivedFrom":[subQ1,subQ0]});Q39=makeQuery(id+"F21.imprint","IMPRINT",FACE,{"disambiguationData":[TD([[makeQuery(id+"F21.imprint","IMPRINT",EDGE,{"disambiguationData":[TD([[subQ2,-1.0]])],"derivedFrom":subQ1}),-1.0]])]});}
            var Q40;
            Q40=makeQuery(id+"F21.imprint","IMPRINT",FACE,{"disambiguationData":[TD([[makeQuery(id+"F21.imprint","IMPRINT",EDGE,{"derivedFrom":sQuery(id+"F21.wireOp",EDGE,"E33.281")}),1.0]])]});
            var Q41;
            {var subQ0=sQuery(id+"F21.wireOp",EDGE,"E33.201");var subQ1=sQuery(id+"F21.wireOp",EDGE,"E33.107");var subQ2=makeQuery(id+"F21.imprint","INTERSECT",VERTEX,{"derivedFrom":[subQ1,subQ0]});Q41=makeQuery(id+"F21.imprint","IMPRINT",FACE,{"disambiguationData":[TD([[makeQuery(id+"F21.imprint","IMPRINT",EDGE,{"disambiguationData":[TD([[subQ2,1.0]])],"derivedFrom":subQ1}),-1.0]])]});}
            extrude(context, id + "F22", {"entities" : qUnion([Q0, Q1, Q2, Q3, Q4, Q5, Q6, Q7, Q8, Q9, Q10, Q11, Q12, Q13, Q14, Q15, Q16, Q17, Q18, Q19, Q20, Q21, Q22, Q23, Q24, Q25, Q26, Q27, Q28, Q29, Q30, Q31, Q32, Q33, Q34, Q35, Q36, Q37, Q38, Q39, Q40, Q41]), "operationType" : NewBodyOperationType.REMOVE, "oppositeDirection" : true, "depth" : 25 * mm, "hasDraft" : true, "draftAngle" : 0.1 * degree});
        }
    });
